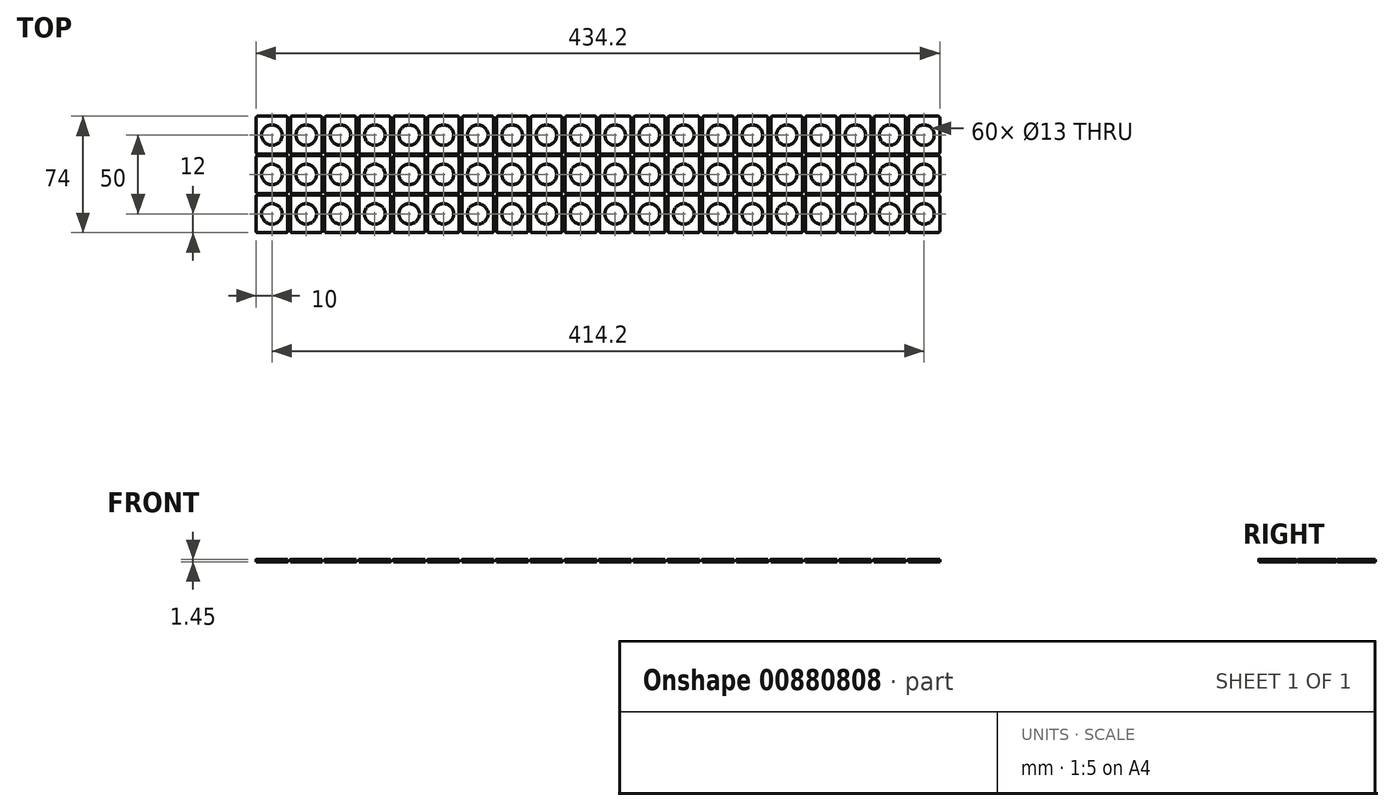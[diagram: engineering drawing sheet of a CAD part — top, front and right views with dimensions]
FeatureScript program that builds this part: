
annotation { "Feature Type Name" : "Feature", "Feature Type Description" : "" }
export const myFeature = defineFeature(function(context is Context, id is Id, definition is map)
    precondition{}
    {
        {
            var Q0;
            Q0=qCreatedBy(makeId("Top.planeOp"),FACE);
            var sketch = newSketch(context, id + "F0", { "sketchPlane" : qUnion([Q0])});
            skLineSegment(sketch, "E0.bottom", {"start": v(-234, 135) * mm, "end": v(-216, 135) * mm});
            skLineSegment(sketch, "E0.top", {"start": v(-234, 111) * mm, "end": v(-216, 111) * mm});
            skLineSegment(sketch, "E0.left", {"start": v(-235, 134) * mm, "end": v(-235, 112) * mm});
            skLineSegment(sketch, "E0.right", {"start": v(-215, 134) * mm, "end": v(-215, 112) * mm});
            skPoint(sketch, "E1.visualSharp", {"position": v(-215, 135) * mm});
            skArc(sketch, "E1.filletArc", {"start": v(-215, 134) * mm, "mid": v(-215.3, 134.7) * mm, "end": v(-216, 135) * mm});
            skPoint(sketch, "E2.visualSharp", {"position": v(-215, 111) * mm});
            skArc(sketch, "E2.filletArc", {"start": v(-216, 111) * mm, "mid": v(-215.3, 111.3) * mm, "end": v(-215, 112) * mm});
            skPoint(sketch, "E3.visualSharp", {"position": v(-235, 111) * mm});
            skArc(sketch, "E3.filletArc", {"start": v(-235, 112) * mm, "mid": v(-234.7, 111.3) * mm, "end": v(-234, 111) * mm});
            skPoint(sketch, "E4.visualSharp", {"position": v(-235, 135) * mm});
            skArc(sketch, "E4.filletArc", {"start": v(-234, 135) * mm, "mid": v(-234.7, 134.7) * mm, "end": v(-235, 134) * mm});
            skLineSegment(sketch, "E5", {"start": v(-215, 123) * mm, "end": v(-235, 123) * mm, "construction": true});
            skCircle(sketch, "E6", {"center": v(-225, 123) * mm, "radius": 6.5 * mm});
            skLineSegment(sketch, "E7.0.1.0", {"start": v(-215, 98) * mm, "end": v(-235, 98) * mm, "construction": true});
            skPoint(sketch, "E7.0.1.1", {"position": v(-235, 110) * mm});
            skLineSegment(sketch, "E7.0.1.2", {"start": v(-235, 109) * mm, "end": v(-235, 87) * mm});
            skPoint(sketch, "E7.0.1.3", {"position": v(-215, 110) * mm});
            skLineSegment(sketch, "E7.0.1.4", {"start": v(-234, 86) * mm, "end": v(-216, 86) * mm});
            skPoint(sketch, "E7.0.1.5", {"position": v(-235, 86) * mm});
            skPoint(sketch, "E7.0.1.6", {"position": v(-215, 86) * mm});
            skCircle(sketch, "E7.0.1.7", {"center": v(-225, 98) * mm, "radius": 6.5 * mm});
            skLineSegment(sketch, "E7.0.1.8", {"start": v(-234, 110) * mm, "end": v(-216, 110) * mm});
            skLineSegment(sketch, "E7.0.1.9", {"start": v(-215, 109) * mm, "end": v(-215, 87) * mm});
            skArc(sketch, "E7.0.1.10", {"start": v(-215, 109) * mm, "mid": v(-215.3, 109.7) * mm, "end": v(-216, 110) * mm});
            skArc(sketch, "E7.0.1.11", {"start": v(-216, 86) * mm, "mid": v(-215.3, 86.3) * mm, "end": v(-215, 87) * mm});
            skArc(sketch, "E7.0.1.12", {"start": v(-235, 87) * mm, "mid": v(-234.7, 86.3) * mm, "end": v(-234, 86) * mm});
            skArc(sketch, "E7.0.1.13", {"start": v(-234, 110) * mm, "mid": v(-234.7, 109.7) * mm, "end": v(-235, 109) * mm});
            skLineSegment(sketch, "E7.0.2.0", {"start": v(-215, 73) * mm, "end": v(-235, 73) * mm, "construction": true});
            skPoint(sketch, "E7.0.2.1", {"position": v(-235, 85) * mm});
            skLineSegment(sketch, "E7.0.2.2", {"start": v(-235, 84) * mm, "end": v(-235, 62) * mm});
            skPoint(sketch, "E7.0.2.3", {"position": v(-215, 85) * mm});
            skLineSegment(sketch, "E7.0.2.4", {"start": v(-234, 61) * mm, "end": v(-216, 61) * mm});
            skPoint(sketch, "E7.0.2.5", {"position": v(-235, 61) * mm});
            skPoint(sketch, "E7.0.2.6", {"position": v(-215, 61) * mm});
            skCircle(sketch, "E7.0.2.7", {"center": v(-225, 73) * mm, "radius": 6.5 * mm});
            skLineSegment(sketch, "E7.0.2.8", {"start": v(-234, 85) * mm, "end": v(-216, 85) * mm});
            skLineSegment(sketch, "E7.0.2.9", {"start": v(-215, 84) * mm, "end": v(-215, 62) * mm});
            skArc(sketch, "E7.0.2.10", {"start": v(-215, 84) * mm, "mid": v(-215.3, 84.7) * mm, "end": v(-216, 85) * mm});
            skArc(sketch, "E7.0.2.11", {"start": v(-216, 61) * mm, "mid": v(-215.3, 61.3) * mm, "end": v(-215, 62) * mm});
            skArc(sketch, "E7.0.2.12", {"start": v(-235, 62) * mm, "mid": v(-234.7, 61.3) * mm, "end": v(-234, 61) * mm});
            skArc(sketch, "E7.0.2.13", {"start": v(-234, 85) * mm, "mid": v(-234.7, 84.7) * mm, "end": v(-235, 84) * mm});
            skLineSegment(sketch, "E7.1.0.0", {"start": v(-193.2, 123) * mm, "end": v(-213.2, 123) * mm, "construction": true});
            skPoint(sketch, "E7.1.0.1", {"position": v(-213.2, 135) * mm});
            skLineSegment(sketch, "E7.1.0.2", {"start": v(-213.2, 134) * mm, "end": v(-213.2, 112) * mm});
            skPoint(sketch, "E7.1.0.3", {"position": v(-193.2, 135) * mm});
            skLineSegment(sketch, "E7.1.0.4", {"start": v(-212.2, 111) * mm, "end": v(-194.2, 111) * mm});
            skPoint(sketch, "E7.1.0.5", {"position": v(-213.2, 111) * mm});
            skPoint(sketch, "E7.1.0.6", {"position": v(-193.2, 111) * mm});
            skCircle(sketch, "E7.1.0.7", {"center": v(-203.2, 123) * mm, "radius": 6.5 * mm});
            skLineSegment(sketch, "E7.1.0.8", {"start": v(-212.2, 135) * mm, "end": v(-194.2, 135) * mm});
            skLineSegment(sketch, "E7.1.0.9", {"start": v(-193.2, 134) * mm, "end": v(-193.2, 112) * mm});
            skArc(sketch, "E7.1.0.10", {"start": v(-193.2, 134) * mm, "mid": v(-193.5, 134.7) * mm, "end": v(-194.2, 135) * mm});
            skArc(sketch, "E7.1.0.11", {"start": v(-194.2, 111) * mm, "mid": v(-193.5, 111.3) * mm, "end": v(-193.2, 112) * mm});
            skArc(sketch, "E7.1.0.12", {"start": v(-213.2, 112) * mm, "mid": v(-212.9, 111.3) * mm, "end": v(-212.2, 111) * mm});
            skArc(sketch, "E7.1.0.13", {"start": v(-212.2, 135) * mm, "mid": v(-212.9, 134.7) * mm, "end": v(-213.2, 134) * mm});
            skLineSegment(sketch, "E7.1.1.0", {"start": v(-193.2, 98) * mm, "end": v(-213.2, 98) * mm, "construction": true});
            skPoint(sketch, "E7.1.1.1", {"position": v(-213.2, 110) * mm});
            skLineSegment(sketch, "E7.1.1.2", {"start": v(-213.2, 109) * mm, "end": v(-213.2, 87) * mm});
            skPoint(sketch, "E7.1.1.3", {"position": v(-193.2, 110) * mm});
            skLineSegment(sketch, "E7.1.1.4", {"start": v(-212.2, 86) * mm, "end": v(-194.2, 86) * mm});
            skPoint(sketch, "E7.1.1.5", {"position": v(-213.2, 86) * mm});
            skPoint(sketch, "E7.1.1.6", {"position": v(-193.2, 86) * mm});
            skCircle(sketch, "E7.1.1.7", {"center": v(-203.2, 98) * mm, "radius": 6.5 * mm});
            skLineSegment(sketch, "E7.1.1.8", {"start": v(-212.2, 110) * mm, "end": v(-194.2, 110) * mm});
            skLineSegment(sketch, "E7.1.1.9", {"start": v(-193.2, 109) * mm, "end": v(-193.2, 87) * mm});
            skArc(sketch, "E7.1.1.10", {"start": v(-193.2, 109) * mm, "mid": v(-193.5, 109.7) * mm, "end": v(-194.2, 110) * mm});
            skArc(sketch, "E7.1.1.11", {"start": v(-194.2, 86) * mm, "mid": v(-193.5, 86.3) * mm, "end": v(-193.2, 87) * mm});
            skArc(sketch, "E7.1.1.12", {"start": v(-213.2, 87) * mm, "mid": v(-212.9, 86.3) * mm, "end": v(-212.2, 86) * mm});
            skArc(sketch, "E7.1.1.13", {"start": v(-212.2, 110) * mm, "mid": v(-212.9, 109.7) * mm, "end": v(-213.2, 109) * mm});
            skLineSegment(sketch, "E7.1.2.0", {"start": v(-193.2, 73) * mm, "end": v(-213.2, 73) * mm, "construction": true});
            skPoint(sketch, "E7.1.2.1", {"position": v(-213.2, 85) * mm});
            skLineSegment(sketch, "E7.1.2.2", {"start": v(-213.2, 84) * mm, "end": v(-213.2, 62) * mm});
            skPoint(sketch, "E7.1.2.3", {"position": v(-193.2, 85) * mm});
            skLineSegment(sketch, "E7.1.2.4", {"start": v(-212.2, 61) * mm, "end": v(-194.2, 61) * mm});
            skPoint(sketch, "E7.1.2.5", {"position": v(-213.2, 61) * mm});
            skPoint(sketch, "E7.1.2.6", {"position": v(-193.2, 61) * mm});
            skCircle(sketch, "E7.1.2.7", {"center": v(-203.2, 73) * mm, "radius": 6.5 * mm});
            skLineSegment(sketch, "E7.1.2.8", {"start": v(-212.2, 85) * mm, "end": v(-194.2, 85) * mm});
            skLineSegment(sketch, "E7.1.2.9", {"start": v(-193.2, 84) * mm, "end": v(-193.2, 62) * mm});
            skArc(sketch, "E7.1.2.10", {"start": v(-193.2, 84) * mm, "mid": v(-193.5, 84.7) * mm, "end": v(-194.2, 85) * mm});
            skArc(sketch, "E7.1.2.11", {"start": v(-194.2, 61) * mm, "mid": v(-193.5, 61.3) * mm, "end": v(-193.2, 62) * mm});
            skArc(sketch, "E7.1.2.12", {"start": v(-213.2, 62) * mm, "mid": v(-212.9, 61.3) * mm, "end": v(-212.2, 61) * mm});
            skArc(sketch, "E7.1.2.13", {"start": v(-212.2, 85) * mm, "mid": v(-212.9, 84.7) * mm, "end": v(-213.2, 84) * mm});
            skLineSegment(sketch, "E7.2.0.0", {"start": v(-171.4, 123) * mm, "end": v(-191.4, 123) * mm, "construction": true});
            skPoint(sketch, "E7.2.0.1", {"position": v(-191.4, 135) * mm});
            skLineSegment(sketch, "E7.2.0.2", {"start": v(-191.4, 134) * mm, "end": v(-191.4, 112) * mm});
            skPoint(sketch, "E7.2.0.3", {"position": v(-171.4, 135) * mm});
            skLineSegment(sketch, "E7.2.0.4", {"start": v(-190.4, 111) * mm, "end": v(-172.4, 111) * mm});
            skPoint(sketch, "E7.2.0.5", {"position": v(-191.4, 111) * mm});
            skPoint(sketch, "E7.2.0.6", {"position": v(-171.4, 111) * mm});
            skCircle(sketch, "E7.2.0.7", {"center": v(-181.4, 123) * mm, "radius": 6.5 * mm});
            skLineSegment(sketch, "E7.2.0.8", {"start": v(-190.4, 135) * mm, "end": v(-172.4, 135) * mm});
            skLineSegment(sketch, "E7.2.0.9", {"start": v(-171.4, 134) * mm, "end": v(-171.4, 112) * mm});
            skArc(sketch, "E7.2.0.10", {"start": v(-171.4, 134) * mm, "mid": v(-171.7, 134.7) * mm, "end": v(-172.4, 135) * mm});
            skArc(sketch, "E7.2.0.11", {"start": v(-172.4, 111) * mm, "mid": v(-171.7, 111.3) * mm, "end": v(-171.4, 112) * mm});
            skArc(sketch, "E7.2.0.12", {"start": v(-191.4, 112) * mm, "mid": v(-191.1, 111.3) * mm, "end": v(-190.4, 111) * mm});
            skArc(sketch, "E7.2.0.13", {"start": v(-190.4, 135) * mm, "mid": v(-191.1, 134.7) * mm, "end": v(-191.4, 134) * mm});
            skLineSegment(sketch, "E7.2.1.0", {"start": v(-171.4, 98) * mm, "end": v(-191.4, 98) * mm, "construction": true});
            skPoint(sketch, "E7.2.1.1", {"position": v(-191.4, 110) * mm});
            skLineSegment(sketch, "E7.2.1.2", {"start": v(-191.4, 109) * mm, "end": v(-191.4, 87) * mm});
            skPoint(sketch, "E7.2.1.3", {"position": v(-171.4, 110) * mm});
            skLineSegment(sketch, "E7.2.1.4", {"start": v(-190.4, 86) * mm, "end": v(-172.4, 86) * mm});
            skPoint(sketch, "E7.2.1.5", {"position": v(-191.4, 86) * mm});
            skPoint(sketch, "E7.2.1.6", {"position": v(-171.4, 86) * mm});
            skCircle(sketch, "E7.2.1.7", {"center": v(-181.4, 98) * mm, "radius": 6.5 * mm});
            skLineSegment(sketch, "E7.2.1.8", {"start": v(-190.4, 110) * mm, "end": v(-172.4, 110) * mm});
            skLineSegment(sketch, "E7.2.1.9", {"start": v(-171.4, 109) * mm, "end": v(-171.4, 87) * mm});
            skArc(sketch, "E7.2.1.10", {"start": v(-171.4, 109) * mm, "mid": v(-171.7, 109.7) * mm, "end": v(-172.4, 110) * mm});
            skArc(sketch, "E7.2.1.11", {"start": v(-172.4, 86) * mm, "mid": v(-171.7, 86.3) * mm, "end": v(-171.4, 87) * mm});
            skArc(sketch, "E7.2.1.12", {"start": v(-191.4, 87) * mm, "mid": v(-191.1, 86.3) * mm, "end": v(-190.4, 86) * mm});
            skArc(sketch, "E7.2.1.13", {"start": v(-190.4, 110) * mm, "mid": v(-191.1, 109.7) * mm, "end": v(-191.4, 109) * mm});
            skLineSegment(sketch, "E7.2.2.0", {"start": v(-171.4, 73) * mm, "end": v(-191.4, 73) * mm, "construction": true});
            skPoint(sketch, "E7.2.2.1", {"position": v(-191.4, 85) * mm});
            skLineSegment(sketch, "E7.2.2.2", {"start": v(-191.4, 84) * mm, "end": v(-191.4, 62) * mm});
            skPoint(sketch, "E7.2.2.3", {"position": v(-171.4, 85) * mm});
            skLineSegment(sketch, "E7.2.2.4", {"start": v(-190.4, 61) * mm, "end": v(-172.4, 61) * mm});
            skPoint(sketch, "E7.2.2.5", {"position": v(-191.4, 61) * mm});
            skPoint(sketch, "E7.2.2.6", {"position": v(-171.4, 61) * mm});
            skCircle(sketch, "E7.2.2.7", {"center": v(-181.4, 73) * mm, "radius": 6.5 * mm});
            skLineSegment(sketch, "E7.2.2.8", {"start": v(-190.4, 85) * mm, "end": v(-172.4, 85) * mm});
            skLineSegment(sketch, "E7.2.2.9", {"start": v(-171.4, 84) * mm, "end": v(-171.4, 62) * mm});
            skArc(sketch, "E7.2.2.10", {"start": v(-171.4, 84) * mm, "mid": v(-171.7, 84.7) * mm, "end": v(-172.4, 85) * mm});
            skArc(sketch, "E7.2.2.11", {"start": v(-172.4, 61) * mm, "mid": v(-171.7, 61.3) * mm, "end": v(-171.4, 62) * mm});
            skArc(sketch, "E7.2.2.12", {"start": v(-191.4, 62) * mm, "mid": v(-191.1, 61.3) * mm, "end": v(-190.4, 61) * mm});
            skArc(sketch, "E7.2.2.13", {"start": v(-190.4, 85) * mm, "mid": v(-191.1, 84.7) * mm, "end": v(-191.4, 84) * mm});
            skLineSegment(sketch, "E7.3.0.0", {"start": v(-149.6, 123) * mm, "end": v(-169.6, 123) * mm, "construction": true});
            skPoint(sketch, "E7.3.0.1", {"position": v(-169.6, 135) * mm});
            skLineSegment(sketch, "E7.3.0.2", {"start": v(-169.6, 134) * mm, "end": v(-169.6, 112) * mm});
            skPoint(sketch, "E7.3.0.3", {"position": v(-149.6, 135) * mm});
            skLineSegment(sketch, "E7.3.0.4", {"start": v(-168.6, 111) * mm, "end": v(-150.6, 111) * mm});
            skPoint(sketch, "E7.3.0.5", {"position": v(-169.6, 111) * mm});
            skPoint(sketch, "E7.3.0.6", {"position": v(-149.6, 111) * mm});
            skCircle(sketch, "E7.3.0.7", {"center": v(-159.6, 123) * mm, "radius": 6.5 * mm});
            skLineSegment(sketch, "E7.3.0.8", {"start": v(-168.6, 135) * mm, "end": v(-150.6, 135) * mm});
            skLineSegment(sketch, "E7.3.0.9", {"start": v(-149.6, 134) * mm, "end": v(-149.6, 112) * mm});
            skArc(sketch, "E7.3.0.10", {"start": v(-149.6, 134) * mm, "mid": v(-149.9, 134.7) * mm, "end": v(-150.6, 135) * mm});
            skArc(sketch, "E7.3.0.11", {"start": v(-150.6, 111) * mm, "mid": v(-149.9, 111.3) * mm, "end": v(-149.6, 112) * mm});
            skArc(sketch, "E7.3.0.12", {"start": v(-169.6, 112) * mm, "mid": v(-169.3, 111.3) * mm, "end": v(-168.6, 111) * mm});
            skArc(sketch, "E7.3.0.13", {"start": v(-168.6, 135) * mm, "mid": v(-169.3, 134.7) * mm, "end": v(-169.6, 134) * mm});
            skLineSegment(sketch, "E7.3.1.0", {"start": v(-149.6, 98) * mm, "end": v(-169.6, 98) * mm, "construction": true});
            skPoint(sketch, "E7.3.1.1", {"position": v(-169.6, 110) * mm});
            skLineSegment(sketch, "E7.3.1.2", {"start": v(-169.6, 109) * mm, "end": v(-169.6, 87) * mm});
            skPoint(sketch, "E7.3.1.3", {"position": v(-149.6, 110) * mm});
            skLineSegment(sketch, "E7.3.1.4", {"start": v(-168.6, 86) * mm, "end": v(-150.6, 86) * mm});
            skPoint(sketch, "E7.3.1.5", {"position": v(-169.6, 86) * mm});
            skPoint(sketch, "E7.3.1.6", {"position": v(-149.6, 86) * mm});
            skCircle(sketch, "E7.3.1.7", {"center": v(-159.6, 98) * mm, "radius": 6.5 * mm});
            skLineSegment(sketch, "E7.3.1.8", {"start": v(-168.6, 110) * mm, "end": v(-150.6, 110) * mm});
            skLineSegment(sketch, "E7.3.1.9", {"start": v(-149.6, 109) * mm, "end": v(-149.6, 87) * mm});
            skArc(sketch, "E7.3.1.10", {"start": v(-149.6, 109) * mm, "mid": v(-149.9, 109.7) * mm, "end": v(-150.6, 110) * mm});
            skArc(sketch, "E7.3.1.11", {"start": v(-150.6, 86) * mm, "mid": v(-149.9, 86.3) * mm, "end": v(-149.6, 87) * mm});
            skArc(sketch, "E7.3.1.12", {"start": v(-169.6, 87) * mm, "mid": v(-169.3, 86.3) * mm, "end": v(-168.6, 86) * mm});
            skArc(sketch, "E7.3.1.13", {"start": v(-168.6, 110) * mm, "mid": v(-169.3, 109.7) * mm, "end": v(-169.6, 109) * mm});
            skLineSegment(sketch, "E7.3.2.0", {"start": v(-149.6, 73) * mm, "end": v(-169.6, 73) * mm, "construction": true});
            skPoint(sketch, "E7.3.2.1", {"position": v(-169.6, 85) * mm});
            skLineSegment(sketch, "E7.3.2.2", {"start": v(-169.6, 84) * mm, "end": v(-169.6, 62) * mm});
            skPoint(sketch, "E7.3.2.3", {"position": v(-149.6, 85) * mm});
            skLineSegment(sketch, "E7.3.2.4", {"start": v(-168.6, 61) * mm, "end": v(-150.6, 61) * mm});
            skPoint(sketch, "E7.3.2.5", {"position": v(-169.6, 61) * mm});
            skPoint(sketch, "E7.3.2.6", {"position": v(-149.6, 61) * mm});
            skCircle(sketch, "E7.3.2.7", {"center": v(-159.6, 73) * mm, "radius": 6.5 * mm});
            skLineSegment(sketch, "E7.3.2.8", {"start": v(-168.6, 85) * mm, "end": v(-150.6, 85) * mm});
            skLineSegment(sketch, "E7.3.2.9", {"start": v(-149.6, 84) * mm, "end": v(-149.6, 62) * mm});
            skArc(sketch, "E7.3.2.10", {"start": v(-149.6, 84) * mm, "mid": v(-149.9, 84.7) * mm, "end": v(-150.6, 85) * mm});
            skArc(sketch, "E7.3.2.11", {"start": v(-150.6, 61) * mm, "mid": v(-149.9, 61.3) * mm, "end": v(-149.6, 62) * mm});
            skArc(sketch, "E7.3.2.12", {"start": v(-169.6, 62) * mm, "mid": v(-169.3, 61.3) * mm, "end": v(-168.6, 61) * mm});
            skArc(sketch, "E7.3.2.13", {"start": v(-168.6, 85) * mm, "mid": v(-169.3, 84.7) * mm, "end": v(-169.6, 84) * mm});
            skLineSegment(sketch, "E7.4.0.0", {"start": v(-127.8, 123) * mm, "end": v(-147.8, 123) * mm, "construction": true});
            skPoint(sketch, "E7.4.0.1", {"position": v(-147.8, 135) * mm});
            skLineSegment(sketch, "E7.4.0.2", {"start": v(-147.8, 134) * mm, "end": v(-147.8, 112) * mm});
            skPoint(sketch, "E7.4.0.3", {"position": v(-127.8, 135) * mm});
            skLineSegment(sketch, "E7.4.0.4", {"start": v(-146.8, 111) * mm, "end": v(-128.8, 111) * mm});
            skPoint(sketch, "E7.4.0.5", {"position": v(-147.8, 111) * mm});
            skPoint(sketch, "E7.4.0.6", {"position": v(-127.8, 111) * mm});
            skCircle(sketch, "E7.4.0.7", {"center": v(-137.8, 123) * mm, "radius": 6.5 * mm});
            skLineSegment(sketch, "E7.4.0.8", {"start": v(-146.8, 135) * mm, "end": v(-128.8, 135) * mm});
            skLineSegment(sketch, "E7.4.0.9", {"start": v(-127.8, 134) * mm, "end": v(-127.8, 112) * mm});
            skArc(sketch, "E7.4.0.10", {"start": v(-127.8, 134) * mm, "mid": v(-128.1, 134.7) * mm, "end": v(-128.8, 135) * mm});
            skArc(sketch, "E7.4.0.11", {"start": v(-128.8, 111) * mm, "mid": v(-128.1, 111.3) * mm, "end": v(-127.8, 112) * mm});
            skArc(sketch, "E7.4.0.12", {"start": v(-147.8, 112) * mm, "mid": v(-147.5, 111.3) * mm, "end": v(-146.8, 111) * mm});
            skArc(sketch, "E7.4.0.13", {"start": v(-146.8, 135) * mm, "mid": v(-147.5, 134.7) * mm, "end": v(-147.8, 134) * mm});
            skLineSegment(sketch, "E7.4.1.0", {"start": v(-127.8, 98) * mm, "end": v(-147.8, 98) * mm, "construction": true});
            skPoint(sketch, "E7.4.1.1", {"position": v(-147.8, 110) * mm});
            skLineSegment(sketch, "E7.4.1.2", {"start": v(-147.8, 109) * mm, "end": v(-147.8, 87) * mm});
            skPoint(sketch, "E7.4.1.3", {"position": v(-127.8, 110) * mm});
            skLineSegment(sketch, "E7.4.1.4", {"start": v(-146.8, 86) * mm, "end": v(-128.8, 86) * mm});
            skPoint(sketch, "E7.4.1.5", {"position": v(-147.8, 86) * mm});
            skPoint(sketch, "E7.4.1.6", {"position": v(-127.8, 86) * mm});
            skCircle(sketch, "E7.4.1.7", {"center": v(-137.8, 98) * mm, "radius": 6.5 * mm});
            skLineSegment(sketch, "E7.4.1.8", {"start": v(-146.8, 110) * mm, "end": v(-128.8, 110) * mm});
            skLineSegment(sketch, "E7.4.1.9", {"start": v(-127.8, 109) * mm, "end": v(-127.8, 87) * mm});
            skArc(sketch, "E7.4.1.10", {"start": v(-127.8, 109) * mm, "mid": v(-128.1, 109.7) * mm, "end": v(-128.8, 110) * mm});
            skArc(sketch, "E7.4.1.11", {"start": v(-128.8, 86) * mm, "mid": v(-128.1, 86.3) * mm, "end": v(-127.8, 87) * mm});
            skArc(sketch, "E7.4.1.12", {"start": v(-147.8, 87) * mm, "mid": v(-147.5, 86.3) * mm, "end": v(-146.8, 86) * mm});
            skArc(sketch, "E7.4.1.13", {"start": v(-146.8, 110) * mm, "mid": v(-147.5, 109.7) * mm, "end": v(-147.8, 109) * mm});
            skLineSegment(sketch, "E7.4.2.0", {"start": v(-127.8, 73) * mm, "end": v(-147.8, 73) * mm, "construction": true});
            skPoint(sketch, "E7.4.2.1", {"position": v(-147.8, 85) * mm});
            skLineSegment(sketch, "E7.4.2.2", {"start": v(-147.8, 84) * mm, "end": v(-147.8, 62) * mm});
            skPoint(sketch, "E7.4.2.3", {"position": v(-127.8, 85) * mm});
            skLineSegment(sketch, "E7.4.2.4", {"start": v(-146.8, 61) * mm, "end": v(-128.8, 61) * mm});
            skPoint(sketch, "E7.4.2.5", {"position": v(-147.8, 61) * mm});
            skPoint(sketch, "E7.4.2.6", {"position": v(-127.8, 61) * mm});
            skCircle(sketch, "E7.4.2.7", {"center": v(-137.8, 73) * mm, "radius": 6.5 * mm});
            skLineSegment(sketch, "E7.4.2.8", {"start": v(-146.8, 85) * mm, "end": v(-128.8, 85) * mm});
            skLineSegment(sketch, "E7.4.2.9", {"start": v(-127.8, 84) * mm, "end": v(-127.8, 62) * mm});
            skArc(sketch, "E7.4.2.10", {"start": v(-127.8, 84) * mm, "mid": v(-128.1, 84.7) * mm, "end": v(-128.8, 85) * mm});
            skArc(sketch, "E7.4.2.11", {"start": v(-128.8, 61) * mm, "mid": v(-128.1, 61.3) * mm, "end": v(-127.8, 62) * mm});
            skArc(sketch, "E7.4.2.12", {"start": v(-147.8, 62) * mm, "mid": v(-147.5, 61.3) * mm, "end": v(-146.8, 61) * mm});
            skArc(sketch, "E7.4.2.13", {"start": v(-146.8, 85) * mm, "mid": v(-147.5, 84.7) * mm, "end": v(-147.8, 84) * mm});
            skLineSegment(sketch, "E7.5.0.0", {"start": v(-106, 123) * mm, "end": v(-126, 123) * mm, "construction": true});
            skPoint(sketch, "E7.5.0.1", {"position": v(-126, 135) * mm});
            skLineSegment(sketch, "E7.5.0.2", {"start": v(-126, 134) * mm, "end": v(-126, 112) * mm});
            skPoint(sketch, "E7.5.0.3", {"position": v(-106, 135) * mm});
            skLineSegment(sketch, "E7.5.0.4", {"start": v(-125, 111) * mm, "end": v(-107, 111) * mm});
            skPoint(sketch, "E7.5.0.5", {"position": v(-126, 111) * mm});
            skPoint(sketch, "E7.5.0.6", {"position": v(-106, 111) * mm});
            skCircle(sketch, "E7.5.0.7", {"center": v(-116, 123) * mm, "radius": 6.5 * mm});
            skLineSegment(sketch, "E7.5.0.8", {"start": v(-125, 135) * mm, "end": v(-107, 135) * mm});
            skLineSegment(sketch, "E7.5.0.9", {"start": v(-106, 134) * mm, "end": v(-106, 112) * mm});
            skArc(sketch, "E7.5.0.10", {"start": v(-106, 134) * mm, "mid": v(-106.3, 134.7) * mm, "end": v(-107, 135) * mm});
            skArc(sketch, "E7.5.0.11", {"start": v(-107, 111) * mm, "mid": v(-106.3, 111.3) * mm, "end": v(-106, 112) * mm});
            skArc(sketch, "E7.5.0.12", {"start": v(-126, 112) * mm, "mid": v(-125.7, 111.3) * mm, "end": v(-125, 111) * mm});
            skArc(sketch, "E7.5.0.13", {"start": v(-125, 135) * mm, "mid": v(-125.7, 134.7) * mm, "end": v(-126, 134) * mm});
            skLineSegment(sketch, "E7.5.1.0", {"start": v(-106, 98) * mm, "end": v(-126, 98) * mm, "construction": true});
            skPoint(sketch, "E7.5.1.1", {"position": v(-126, 110) * mm});
            skLineSegment(sketch, "E7.5.1.2", {"start": v(-126, 109) * mm, "end": v(-126, 87) * mm});
            skPoint(sketch, "E7.5.1.3", {"position": v(-106, 110) * mm});
            skLineSegment(sketch, "E7.5.1.4", {"start": v(-125, 86) * mm, "end": v(-107, 86) * mm});
            skPoint(sketch, "E7.5.1.5", {"position": v(-126, 86) * mm});
            skPoint(sketch, "E7.5.1.6", {"position": v(-106, 86) * mm});
            skCircle(sketch, "E7.5.1.7", {"center": v(-116, 98) * mm, "radius": 6.5 * mm});
            skLineSegment(sketch, "E7.5.1.8", {"start": v(-125, 110) * mm, "end": v(-107, 110) * mm});
            skLineSegment(sketch, "E7.5.1.9", {"start": v(-106, 109) * mm, "end": v(-106, 87) * mm});
            skArc(sketch, "E7.5.1.10", {"start": v(-106, 109) * mm, "mid": v(-106.3, 109.7) * mm, "end": v(-107, 110) * mm});
            skArc(sketch, "E7.5.1.11", {"start": v(-107, 86) * mm, "mid": v(-106.3, 86.3) * mm, "end": v(-106, 87) * mm});
            skArc(sketch, "E7.5.1.12", {"start": v(-126, 87) * mm, "mid": v(-125.7, 86.3) * mm, "end": v(-125, 86) * mm});
            skArc(sketch, "E7.5.1.13", {"start": v(-125, 110) * mm, "mid": v(-125.7, 109.7) * mm, "end": v(-126, 109) * mm});
            skLineSegment(sketch, "E7.5.2.0", {"start": v(-106, 73) * mm, "end": v(-126, 73) * mm, "construction": true});
            skPoint(sketch, "E7.5.2.1", {"position": v(-126, 85) * mm});
            skLineSegment(sketch, "E7.5.2.2", {"start": v(-126, 84) * mm, "end": v(-126, 62) * mm});
            skPoint(sketch, "E7.5.2.3", {"position": v(-106, 85) * mm});
            skLineSegment(sketch, "E7.5.2.4", {"start": v(-125, 61) * mm, "end": v(-107, 61) * mm});
            skPoint(sketch, "E7.5.2.5", {"position": v(-126, 61) * mm});
            skPoint(sketch, "E7.5.2.6", {"position": v(-106, 61) * mm});
            skCircle(sketch, "E7.5.2.7", {"center": v(-116, 73) * mm, "radius": 6.5 * mm});
            skLineSegment(sketch, "E7.5.2.8", {"start": v(-125, 85) * mm, "end": v(-107, 85) * mm});
            skLineSegment(sketch, "E7.5.2.9", {"start": v(-106, 84) * mm, "end": v(-106, 62) * mm});
            skArc(sketch, "E7.5.2.10", {"start": v(-106, 84) * mm, "mid": v(-106.3, 84.7) * mm, "end": v(-107, 85) * mm});
            skArc(sketch, "E7.5.2.11", {"start": v(-107, 61) * mm, "mid": v(-106.3, 61.3) * mm, "end": v(-106, 62) * mm});
            skArc(sketch, "E7.5.2.12", {"start": v(-126, 62) * mm, "mid": v(-125.7, 61.3) * mm, "end": v(-125, 61) * mm});
            skArc(sketch, "E7.5.2.13", {"start": v(-125, 85) * mm, "mid": v(-125.7, 84.7) * mm, "end": v(-126, 84) * mm});
            skLineSegment(sketch, "E7.6.0.0", {"start": v(-84.2, 123) * mm, "end": v(-104.2, 123) * mm, "construction": true});
            skPoint(sketch, "E7.6.0.1", {"position": v(-104.2, 135) * mm});
            skLineSegment(sketch, "E7.6.0.2", {"start": v(-104.2, 134) * mm, "end": v(-104.2, 112) * mm});
            skPoint(sketch, "E7.6.0.3", {"position": v(-84.2, 135) * mm});
            skLineSegment(sketch, "E7.6.0.4", {"start": v(-103.2, 111) * mm, "end": v(-85.2, 111) * mm});
            skPoint(sketch, "E7.6.0.5", {"position": v(-104.2, 111) * mm});
            skPoint(sketch, "E7.6.0.6", {"position": v(-84.2, 111) * mm});
            skCircle(sketch, "E7.6.0.7", {"center": v(-94.2, 123) * mm, "radius": 6.5 * mm});
            skLineSegment(sketch, "E7.6.0.8", {"start": v(-103.2, 135) * mm, "end": v(-85.2, 135) * mm});
            skLineSegment(sketch, "E7.6.0.9", {"start": v(-84.2, 134) * mm, "end": v(-84.2, 112) * mm});
            skArc(sketch, "E7.6.0.10", {"start": v(-84.2, 134) * mm, "mid": v(-84.5, 134.7) * mm, "end": v(-85.2, 135) * mm});
            skArc(sketch, "E7.6.0.11", {"start": v(-85.2, 111) * mm, "mid": v(-84.5, 111.3) * mm, "end": v(-84.2, 112) * mm});
            skArc(sketch, "E7.6.0.12", {"start": v(-104.2, 112) * mm, "mid": v(-103.9, 111.3) * mm, "end": v(-103.2, 111) * mm});
            skArc(sketch, "E7.6.0.13", {"start": v(-103.2, 135) * mm, "mid": v(-103.9, 134.7) * mm, "end": v(-104.2, 134) * mm});
            skLineSegment(sketch, "E7.6.1.0", {"start": v(-84.2, 98) * mm, "end": v(-104.2, 98) * mm, "construction": true});
            skPoint(sketch, "E7.6.1.1", {"position": v(-104.2, 110) * mm});
            skLineSegment(sketch, "E7.6.1.2", {"start": v(-104.2, 109) * mm, "end": v(-104.2, 87) * mm});
            skPoint(sketch, "E7.6.1.3", {"position": v(-84.2, 110) * mm});
            skLineSegment(sketch, "E7.6.1.4", {"start": v(-103.2, 86) * mm, "end": v(-85.2, 86) * mm});
            skPoint(sketch, "E7.6.1.5", {"position": v(-104.2, 86) * mm});
            skPoint(sketch, "E7.6.1.6", {"position": v(-84.2, 86) * mm});
            skCircle(sketch, "E7.6.1.7", {"center": v(-94.2, 98) * mm, "radius": 6.5 * mm});
            skLineSegment(sketch, "E7.6.1.8", {"start": v(-103.2, 110) * mm, "end": v(-85.2, 110) * mm});
            skLineSegment(sketch, "E7.6.1.9", {"start": v(-84.2, 109) * mm, "end": v(-84.2, 87) * mm});
            skArc(sketch, "E7.6.1.10", {"start": v(-84.2, 109) * mm, "mid": v(-84.5, 109.7) * mm, "end": v(-85.2, 110) * mm});
            skArc(sketch, "E7.6.1.11", {"start": v(-85.2, 86) * mm, "mid": v(-84.5, 86.3) * mm, "end": v(-84.2, 87) * mm});
            skArc(sketch, "E7.6.1.12", {"start": v(-104.2, 87) * mm, "mid": v(-103.9, 86.3) * mm, "end": v(-103.2, 86) * mm});
            skArc(sketch, "E7.6.1.13", {"start": v(-103.2, 110) * mm, "mid": v(-103.9, 109.7) * mm, "end": v(-104.2, 109) * mm});
            skLineSegment(sketch, "E7.6.2.0", {"start": v(-84.2, 73) * mm, "end": v(-104.2, 73) * mm, "construction": true});
            skPoint(sketch, "E7.6.2.1", {"position": v(-104.2, 85) * mm});
            skLineSegment(sketch, "E7.6.2.2", {"start": v(-104.2, 84) * mm, "end": v(-104.2, 62) * mm});
            skPoint(sketch, "E7.6.2.3", {"position": v(-84.2, 85) * mm});
            skLineSegment(sketch, "E7.6.2.4", {"start": v(-103.2, 61) * mm, "end": v(-85.2, 61) * mm});
            skPoint(sketch, "E7.6.2.5", {"position": v(-104.2, 61) * mm});
            skPoint(sketch, "E7.6.2.6", {"position": v(-84.2, 61) * mm});
            skCircle(sketch, "E7.6.2.7", {"center": v(-94.2, 73) * mm, "radius": 6.5 * mm});
            skLineSegment(sketch, "E7.6.2.8", {"start": v(-103.2, 85) * mm, "end": v(-85.2, 85) * mm});
            skLineSegment(sketch, "E7.6.2.9", {"start": v(-84.2, 84) * mm, "end": v(-84.2, 62) * mm});
            skArc(sketch, "E7.6.2.10", {"start": v(-84.2, 84) * mm, "mid": v(-84.5, 84.7) * mm, "end": v(-85.2, 85) * mm});
            skArc(sketch, "E7.6.2.11", {"start": v(-85.2, 61) * mm, "mid": v(-84.5, 61.3) * mm, "end": v(-84.2, 62) * mm});
            skArc(sketch, "E7.6.2.12", {"start": v(-104.2, 62) * mm, "mid": v(-103.9, 61.3) * mm, "end": v(-103.2, 61) * mm});
            skArc(sketch, "E7.6.2.13", {"start": v(-103.2, 85) * mm, "mid": v(-103.9, 84.7) * mm, "end": v(-104.2, 84) * mm});
            skLineSegment(sketch, "E7.7.0.0", {"start": v(-62.4, 123) * mm, "end": v(-82.4, 123) * mm, "construction": true});
            skPoint(sketch, "E7.7.0.1", {"position": v(-82.4, 135) * mm});
            skLineSegment(sketch, "E7.7.0.2", {"start": v(-82.4, 134) * mm, "end": v(-82.4, 112) * mm});
            skPoint(sketch, "E7.7.0.3", {"position": v(-62.4, 135) * mm});
            skLineSegment(sketch, "E7.7.0.4", {"start": v(-81.4, 111) * mm, "end": v(-63.4, 111) * mm});
            skPoint(sketch, "E7.7.0.5", {"position": v(-82.4, 111) * mm});
            skPoint(sketch, "E7.7.0.6", {"position": v(-62.4, 111) * mm});
            skCircle(sketch, "E7.7.0.7", {"center": v(-72.4, 123) * mm, "radius": 6.5 * mm});
            skLineSegment(sketch, "E7.7.0.8", {"start": v(-81.4, 135) * mm, "end": v(-63.4, 135) * mm});
            skLineSegment(sketch, "E7.7.0.9", {"start": v(-62.4, 134) * mm, "end": v(-62.4, 112) * mm});
            skArc(sketch, "E7.7.0.10", {"start": v(-62.4, 134) * mm, "mid": v(-62.7, 134.7) * mm, "end": v(-63.4, 135) * mm});
            skArc(sketch, "E7.7.0.11", {"start": v(-63.4, 111) * mm, "mid": v(-62.7, 111.3) * mm, "end": v(-62.4, 112) * mm});
            skArc(sketch, "E7.7.0.12", {"start": v(-82.4, 112) * mm, "mid": v(-82.1, 111.3) * mm, "end": v(-81.4, 111) * mm});
            skArc(sketch, "E7.7.0.13", {"start": v(-81.4, 135) * mm, "mid": v(-82.1, 134.7) * mm, "end": v(-82.4, 134) * mm});
            skLineSegment(sketch, "E7.7.1.0", {"start": v(-62.4, 98) * mm, "end": v(-82.4, 98) * mm, "construction": true});
            skPoint(sketch, "E7.7.1.1", {"position": v(-82.4, 110) * mm});
            skLineSegment(sketch, "E7.7.1.2", {"start": v(-82.4, 109) * mm, "end": v(-82.4, 87) * mm});
            skPoint(sketch, "E7.7.1.3", {"position": v(-62.4, 110) * mm});
            skLineSegment(sketch, "E7.7.1.4", {"start": v(-81.4, 86) * mm, "end": v(-63.4, 86) * mm});
            skPoint(sketch, "E7.7.1.5", {"position": v(-82.4, 86) * mm});
            skPoint(sketch, "E7.7.1.6", {"position": v(-62.4, 86) * mm});
            skCircle(sketch, "E7.7.1.7", {"center": v(-72.4, 98) * mm, "radius": 6.5 * mm});
            skLineSegment(sketch, "E7.7.1.8", {"start": v(-81.4, 110) * mm, "end": v(-63.4, 110) * mm});
            skLineSegment(sketch, "E7.7.1.9", {"start": v(-62.4, 109) * mm, "end": v(-62.4, 87) * mm});
            skArc(sketch, "E7.7.1.10", {"start": v(-62.4, 109) * mm, "mid": v(-62.7, 109.7) * mm, "end": v(-63.4, 110) * mm});
            skArc(sketch, "E7.7.1.11", {"start": v(-63.4, 86) * mm, "mid": v(-62.7, 86.3) * mm, "end": v(-62.4, 87) * mm});
            skArc(sketch, "E7.7.1.12", {"start": v(-82.4, 87) * mm, "mid": v(-82.1, 86.3) * mm, "end": v(-81.4, 86) * mm});
            skArc(sketch, "E7.7.1.13", {"start": v(-81.4, 110) * mm, "mid": v(-82.1, 109.7) * mm, "end": v(-82.4, 109) * mm});
            skLineSegment(sketch, "E7.7.2.0", {"start": v(-62.4, 73) * mm, "end": v(-82.4, 73) * mm, "construction": true});
            skPoint(sketch, "E7.7.2.1", {"position": v(-82.4, 85) * mm});
            skLineSegment(sketch, "E7.7.2.2", {"start": v(-82.4, 84) * mm, "end": v(-82.4, 62) * mm});
            skPoint(sketch, "E7.7.2.3", {"position": v(-62.4, 85) * mm});
            skLineSegment(sketch, "E7.7.2.4", {"start": v(-81.4, 61) * mm, "end": v(-63.4, 61) * mm});
            skPoint(sketch, "E7.7.2.5", {"position": v(-82.4, 61) * mm});
            skPoint(sketch, "E7.7.2.6", {"position": v(-62.4, 61) * mm});
            skCircle(sketch, "E7.7.2.7", {"center": v(-72.4, 73) * mm, "radius": 6.5 * mm});
            skLineSegment(sketch, "E7.7.2.8", {"start": v(-81.4, 85) * mm, "end": v(-63.4, 85) * mm});
            skLineSegment(sketch, "E7.7.2.9", {"start": v(-62.4, 84) * mm, "end": v(-62.4, 62) * mm});
            skArc(sketch, "E7.7.2.10", {"start": v(-62.4, 84) * mm, "mid": v(-62.7, 84.7) * mm, "end": v(-63.4, 85) * mm});
            skArc(sketch, "E7.7.2.11", {"start": v(-63.4, 61) * mm, "mid": v(-62.7, 61.3) * mm, "end": v(-62.4, 62) * mm});
            skArc(sketch, "E7.7.2.12", {"start": v(-82.4, 62) * mm, "mid": v(-82.1, 61.3) * mm, "end": v(-81.4, 61) * mm});
            skArc(sketch, "E7.7.2.13", {"start": v(-81.4, 85) * mm, "mid": v(-82.1, 84.7) * mm, "end": v(-82.4, 84) * mm});
            skLineSegment(sketch, "E7.8.0.0", {"start": v(-40.6, 123) * mm, "end": v(-60.6, 123) * mm, "construction": true});
            skPoint(sketch, "E7.8.0.1", {"position": v(-60.6, 135) * mm});
            skLineSegment(sketch, "E7.8.0.2", {"start": v(-60.6, 134) * mm, "end": v(-60.6, 112) * mm});
            skPoint(sketch, "E7.8.0.3", {"position": v(-40.6, 135) * mm});
            skLineSegment(sketch, "E7.8.0.4", {"start": v(-59.6, 111) * mm, "end": v(-41.6, 111) * mm});
            skPoint(sketch, "E7.8.0.5", {"position": v(-60.6, 111) * mm});
            skPoint(sketch, "E7.8.0.6", {"position": v(-40.6, 111) * mm});
            skCircle(sketch, "E7.8.0.7", {"center": v(-50.6, 123) * mm, "radius": 6.5 * mm});
            skLineSegment(sketch, "E7.8.0.8", {"start": v(-59.6, 135) * mm, "end": v(-41.6, 135) * mm});
            skLineSegment(sketch, "E7.8.0.9", {"start": v(-40.6, 134) * mm, "end": v(-40.6, 112) * mm});
            skArc(sketch, "E7.8.0.10", {"start": v(-40.6, 134) * mm, "mid": v(-40.9, 134.7) * mm, "end": v(-41.6, 135) * mm});
            skArc(sketch, "E7.8.0.11", {"start": v(-41.6, 111) * mm, "mid": v(-40.9, 111.3) * mm, "end": v(-40.6, 112) * mm});
            skArc(sketch, "E7.8.0.12", {"start": v(-60.6, 112) * mm, "mid": v(-60.3, 111.3) * mm, "end": v(-59.6, 111) * mm});
            skArc(sketch, "E7.8.0.13", {"start": v(-59.6, 135) * mm, "mid": v(-60.3, 134.7) * mm, "end": v(-60.6, 134) * mm});
            skLineSegment(sketch, "E7.8.1.0", {"start": v(-40.6, 98) * mm, "end": v(-60.6, 98) * mm, "construction": true});
            skPoint(sketch, "E7.8.1.1", {"position": v(-60.6, 110) * mm});
            skLineSegment(sketch, "E7.8.1.2", {"start": v(-60.6, 109) * mm, "end": v(-60.6, 87) * mm});
            skPoint(sketch, "E7.8.1.3", {"position": v(-40.6, 110) * mm});
            skLineSegment(sketch, "E7.8.1.4", {"start": v(-59.6, 86) * mm, "end": v(-41.6, 86) * mm});
            skPoint(sketch, "E7.8.1.5", {"position": v(-60.6, 86) * mm});
            skPoint(sketch, "E7.8.1.6", {"position": v(-40.6, 86) * mm});
            skCircle(sketch, "E7.8.1.7", {"center": v(-50.6, 98) * mm, "radius": 6.5 * mm});
            skLineSegment(sketch, "E7.8.1.8", {"start": v(-59.6, 110) * mm, "end": v(-41.6, 110) * mm});
            skLineSegment(sketch, "E7.8.1.9", {"start": v(-40.6, 109) * mm, "end": v(-40.6, 87) * mm});
            skArc(sketch, "E7.8.1.10", {"start": v(-40.6, 109) * mm, "mid": v(-40.9, 109.7) * mm, "end": v(-41.6, 110) * mm});
            skArc(sketch, "E7.8.1.11", {"start": v(-41.6, 86) * mm, "mid": v(-40.9, 86.3) * mm, "end": v(-40.6, 87) * mm});
            skArc(sketch, "E7.8.1.12", {"start": v(-60.6, 87) * mm, "mid": v(-60.3, 86.3) * mm, "end": v(-59.6, 86) * mm});
            skArc(sketch, "E7.8.1.13", {"start": v(-59.6, 110) * mm, "mid": v(-60.3, 109.7) * mm, "end": v(-60.6, 109) * mm});
            skLineSegment(sketch, "E7.8.2.0", {"start": v(-40.6, 73) * mm, "end": v(-60.6, 73) * mm, "construction": true});
            skPoint(sketch, "E7.8.2.1", {"position": v(-60.6, 85) * mm});
            skLineSegment(sketch, "E7.8.2.2", {"start": v(-60.6, 84) * mm, "end": v(-60.6, 62) * mm});
            skPoint(sketch, "E7.8.2.3", {"position": v(-40.6, 85) * mm});
            skLineSegment(sketch, "E7.8.2.4", {"start": v(-59.6, 61) * mm, "end": v(-41.6, 61) * mm});
            skPoint(sketch, "E7.8.2.5", {"position": v(-60.6, 61) * mm});
            skPoint(sketch, "E7.8.2.6", {"position": v(-40.6, 61) * mm});
            skCircle(sketch, "E7.8.2.7", {"center": v(-50.6, 73) * mm, "radius": 6.5 * mm});
            skLineSegment(sketch, "E7.8.2.8", {"start": v(-59.6, 85) * mm, "end": v(-41.6, 85) * mm});
            skLineSegment(sketch, "E7.8.2.9", {"start": v(-40.6, 84) * mm, "end": v(-40.6, 62) * mm});
            skArc(sketch, "E7.8.2.10", {"start": v(-40.6, 84) * mm, "mid": v(-40.9, 84.7) * mm, "end": v(-41.6, 85) * mm});
            skArc(sketch, "E7.8.2.11", {"start": v(-41.6, 61) * mm, "mid": v(-40.9, 61.3) * mm, "end": v(-40.6, 62) * mm});
            skArc(sketch, "E7.8.2.12", {"start": v(-60.6, 62) * mm, "mid": v(-60.3, 61.3) * mm, "end": v(-59.6, 61) * mm});
            skArc(sketch, "E7.8.2.13", {"start": v(-59.6, 85) * mm, "mid": v(-60.3, 84.7) * mm, "end": v(-60.6, 84) * mm});
            skLineSegment(sketch, "E7.9.0.0", {"start": v(-18.8, 123) * mm, "end": v(-38.8, 123) * mm, "construction": true});
            skPoint(sketch, "E7.9.0.1", {"position": v(-38.8, 135) * mm});
            skLineSegment(sketch, "E7.9.0.2", {"start": v(-38.8, 134) * mm, "end": v(-38.8, 112) * mm});
            skPoint(sketch, "E7.9.0.3", {"position": v(-18.8, 135) * mm});
            skLineSegment(sketch, "E7.9.0.4", {"start": v(-37.8, 111) * mm, "end": v(-19.8, 111) * mm});
            skPoint(sketch, "E7.9.0.5", {"position": v(-38.8, 111) * mm});
            skPoint(sketch, "E7.9.0.6", {"position": v(-18.8, 111) * mm});
            skCircle(sketch, "E7.9.0.7", {"center": v(-28.8, 123) * mm, "radius": 6.5 * mm});
            skLineSegment(sketch, "E7.9.0.8", {"start": v(-37.8, 135) * mm, "end": v(-19.8, 135) * mm});
            skLineSegment(sketch, "E7.9.0.9", {"start": v(-18.8, 134) * mm, "end": v(-18.8, 112) * mm});
            skArc(sketch, "E7.9.0.10", {"start": v(-18.8, 134) * mm, "mid": v(-19.1, 134.7) * mm, "end": v(-19.8, 135) * mm});
            skArc(sketch, "E7.9.0.11", {"start": v(-19.8, 111) * mm, "mid": v(-19.1, 111.3) * mm, "end": v(-18.8, 112) * mm});
            skArc(sketch, "E7.9.0.12", {"start": v(-38.8, 112) * mm, "mid": v(-38.5, 111.3) * mm, "end": v(-37.8, 111) * mm});
            skArc(sketch, "E7.9.0.13", {"start": v(-37.8, 135) * mm, "mid": v(-38.5, 134.7) * mm, "end": v(-38.8, 134) * mm});
            skLineSegment(sketch, "E7.9.1.0", {"start": v(-18.8, 98) * mm, "end": v(-38.8, 98) * mm, "construction": true});
            skPoint(sketch, "E7.9.1.1", {"position": v(-38.8, 110) * mm});
            skLineSegment(sketch, "E7.9.1.2", {"start": v(-38.8, 109) * mm, "end": v(-38.8, 87) * mm});
            skPoint(sketch, "E7.9.1.3", {"position": v(-18.8, 110) * mm});
            skLineSegment(sketch, "E7.9.1.4", {"start": v(-37.8, 86) * mm, "end": v(-19.8, 86) * mm});
            skPoint(sketch, "E7.9.1.5", {"position": v(-38.8, 86) * mm});
            skPoint(sketch, "E7.9.1.6", {"position": v(-18.8, 86) * mm});
            skCircle(sketch, "E7.9.1.7", {"center": v(-28.8, 98) * mm, "radius": 6.5 * mm});
            skLineSegment(sketch, "E7.9.1.8", {"start": v(-37.8, 110) * mm, "end": v(-19.8, 110) * mm});
            skLineSegment(sketch, "E7.9.1.9", {"start": v(-18.8, 109) * mm, "end": v(-18.8, 87) * mm});
            skArc(sketch, "E7.9.1.10", {"start": v(-18.8, 109) * mm, "mid": v(-19.1, 109.7) * mm, "end": v(-19.8, 110) * mm});
            skArc(sketch, "E7.9.1.11", {"start": v(-19.8, 86) * mm, "mid": v(-19.1, 86.3) * mm, "end": v(-18.8, 87) * mm});
            skArc(sketch, "E7.9.1.12", {"start": v(-38.8, 87) * mm, "mid": v(-38.5, 86.3) * mm, "end": v(-37.8, 86) * mm});
            skArc(sketch, "E7.9.1.13", {"start": v(-37.8, 110) * mm, "mid": v(-38.5, 109.7) * mm, "end": v(-38.8, 109) * mm});
            skLineSegment(sketch, "E7.9.2.0", {"start": v(-18.8, 73) * mm, "end": v(-38.8, 73) * mm, "construction": true});
            skPoint(sketch, "E7.9.2.1", {"position": v(-38.8, 85) * mm});
            skLineSegment(sketch, "E7.9.2.2", {"start": v(-38.8, 84) * mm, "end": v(-38.8, 62) * mm});
            skPoint(sketch, "E7.9.2.3", {"position": v(-18.8, 85) * mm});
            skLineSegment(sketch, "E7.9.2.4", {"start": v(-37.8, 61) * mm, "end": v(-19.8, 61) * mm});
            skPoint(sketch, "E7.9.2.5", {"position": v(-38.8, 61) * mm});
            skPoint(sketch, "E7.9.2.6", {"position": v(-18.8, 61) * mm});
            skCircle(sketch, "E7.9.2.7", {"center": v(-28.8, 73) * mm, "radius": 6.5 * mm});
            skLineSegment(sketch, "E7.9.2.8", {"start": v(-37.8, 85) * mm, "end": v(-19.8, 85) * mm});
            skLineSegment(sketch, "E7.9.2.9", {"start": v(-18.8, 84) * mm, "end": v(-18.8, 62) * mm});
            skArc(sketch, "E7.9.2.10", {"start": v(-18.8, 84) * mm, "mid": v(-19.1, 84.7) * mm, "end": v(-19.8, 85) * mm});
            skArc(sketch, "E7.9.2.11", {"start": v(-19.8, 61) * mm, "mid": v(-19.1, 61.3) * mm, "end": v(-18.8, 62) * mm});
            skArc(sketch, "E7.9.2.12", {"start": v(-38.8, 62) * mm, "mid": v(-38.5, 61.3) * mm, "end": v(-37.8, 61) * mm});
            skArc(sketch, "E7.9.2.13", {"start": v(-37.8, 85) * mm, "mid": v(-38.5, 84.7) * mm, "end": v(-38.8, 84) * mm});
            skLineSegment(sketch, "E7.10.0.0", {"start": v(3, 123) * mm, "end": v(-17, 123) * mm, "construction": true});
            skPoint(sketch, "E7.10.0.1", {"position": v(-17, 135) * mm});
            skLineSegment(sketch, "E7.10.0.2", {"start": v(-17, 134) * mm, "end": v(-17, 112) * mm});
            skPoint(sketch, "E7.10.0.3", {"position": v(3, 135) * mm});
            skLineSegment(sketch, "E7.10.0.4", {"start": v(-16, 111) * mm, "end": v(2, 111) * mm});
            skPoint(sketch, "E7.10.0.5", {"position": v(-17, 111) * mm});
            skPoint(sketch, "E7.10.0.6", {"position": v(3, 111) * mm});
            skCircle(sketch, "E7.10.0.7", {"center": v(-7, 123) * mm, "radius": 6.5 * mm});
            skLineSegment(sketch, "E7.10.0.8", {"start": v(-16, 135) * mm, "end": v(2, 135) * mm});
            skLineSegment(sketch, "E7.10.0.9", {"start": v(3, 134) * mm, "end": v(3, 112) * mm});
            skArc(sketch, "E7.10.0.10", {"start": v(3, 134) * mm, "mid": v(2.7, 134.7) * mm, "end": v(2, 135) * mm});
            skArc(sketch, "E7.10.0.11", {"start": v(2, 111) * mm, "mid": v(2.7, 111.3) * mm, "end": v(3, 112) * mm});
            skArc(sketch, "E7.10.0.12", {"start": v(-17, 112) * mm, "mid": v(-16.7, 111.3) * mm, "end": v(-16, 111) * mm});
            skArc(sketch, "E7.10.0.13", {"start": v(-16, 135) * mm, "mid": v(-16.7, 134.7) * mm, "end": v(-17, 134) * mm});
            skLineSegment(sketch, "E7.10.1.0", {"start": v(3, 98) * mm, "end": v(-17, 98) * mm, "construction": true});
            skPoint(sketch, "E7.10.1.1", {"position": v(-17, 110) * mm});
            skLineSegment(sketch, "E7.10.1.2", {"start": v(-17, 109) * mm, "end": v(-17, 87) * mm});
            skPoint(sketch, "E7.10.1.3", {"position": v(3, 110) * mm});
            skLineSegment(sketch, "E7.10.1.4", {"start": v(-16, 86) * mm, "end": v(2, 86) * mm});
            skPoint(sketch, "E7.10.1.5", {"position": v(-17, 86) * mm});
            skPoint(sketch, "E7.10.1.6", {"position": v(3, 86) * mm});
            skCircle(sketch, "E7.10.1.7", {"center": v(-7, 98) * mm, "radius": 6.5 * mm});
            skLineSegment(sketch, "E7.10.1.8", {"start": v(-16, 110) * mm, "end": v(2, 110) * mm});
            skLineSegment(sketch, "E7.10.1.9", {"start": v(3, 109) * mm, "end": v(3, 87) * mm});
            skArc(sketch, "E7.10.1.10", {"start": v(3, 109) * mm, "mid": v(2.7, 109.7) * mm, "end": v(2, 110) * mm});
            skArc(sketch, "E7.10.1.11", {"start": v(2, 86) * mm, "mid": v(2.7, 86.3) * mm, "end": v(3, 87) * mm});
            skArc(sketch, "E7.10.1.12", {"start": v(-17, 87) * mm, "mid": v(-16.7, 86.3) * mm, "end": v(-16, 86) * mm});
            skArc(sketch, "E7.10.1.13", {"start": v(-16, 110) * mm, "mid": v(-16.7, 109.7) * mm, "end": v(-17, 109) * mm});
            skLineSegment(sketch, "E7.10.2.0", {"start": v(3, 73) * mm, "end": v(-17, 73) * mm, "construction": true});
            skPoint(sketch, "E7.10.2.1", {"position": v(-17, 85) * mm});
            skLineSegment(sketch, "E7.10.2.2", {"start": v(-17, 84) * mm, "end": v(-17, 62) * mm});
            skPoint(sketch, "E7.10.2.3", {"position": v(3, 85) * mm});
            skLineSegment(sketch, "E7.10.2.4", {"start": v(-16, 61) * mm, "end": v(2, 61) * mm});
            skPoint(sketch, "E7.10.2.5", {"position": v(-17, 61) * mm});
            skPoint(sketch, "E7.10.2.6", {"position": v(3, 61) * mm});
            skCircle(sketch, "E7.10.2.7", {"center": v(-7, 73) * mm, "radius": 6.5 * mm});
            skLineSegment(sketch, "E7.10.2.8", {"start": v(-16, 85) * mm, "end": v(2, 85) * mm});
            skLineSegment(sketch, "E7.10.2.9", {"start": v(3, 84) * mm, "end": v(3, 62) * mm});
            skArc(sketch, "E7.10.2.10", {"start": v(3, 84) * mm, "mid": v(2.7, 84.7) * mm, "end": v(2, 85) * mm});
            skArc(sketch, "E7.10.2.11", {"start": v(2, 61) * mm, "mid": v(2.7, 61.3) * mm, "end": v(3, 62) * mm});
            skArc(sketch, "E7.10.2.12", {"start": v(-17, 62) * mm, "mid": v(-16.7, 61.3) * mm, "end": v(-16, 61) * mm});
            skArc(sketch, "E7.10.2.13", {"start": v(-16, 85) * mm, "mid": v(-16.7, 84.7) * mm, "end": v(-17, 84) * mm});
            skLineSegment(sketch, "E7.11.0.0", {"start": v(24.8, 123) * mm, "end": v(4.8, 123) * mm, "construction": true});
            skPoint(sketch, "E7.11.0.1", {"position": v(4.8, 135) * mm});
            skLineSegment(sketch, "E7.11.0.2", {"start": v(4.8, 134) * mm, "end": v(4.8, 112) * mm});
            skPoint(sketch, "E7.11.0.3", {"position": v(24.8, 135) * mm});
            skLineSegment(sketch, "E7.11.0.4", {"start": v(5.8, 111) * mm, "end": v(23.8, 111) * mm});
            skPoint(sketch, "E7.11.0.5", {"position": v(4.8, 111) * mm});
            skPoint(sketch, "E7.11.0.6", {"position": v(24.8, 111) * mm});
            skCircle(sketch, "E7.11.0.7", {"center": v(14.8, 123) * mm, "radius": 6.5 * mm});
            skLineSegment(sketch, "E7.11.0.8", {"start": v(5.8, 135) * mm, "end": v(23.8, 135) * mm});
            skLineSegment(sketch, "E7.11.0.9", {"start": v(24.8, 134) * mm, "end": v(24.8, 112) * mm});
            skArc(sketch, "E7.11.0.10", {"start": v(24.8, 134) * mm, "mid": v(24.5, 134.7) * mm, "end": v(23.8, 135) * mm});
            skArc(sketch, "E7.11.0.11", {"start": v(23.8, 111) * mm, "mid": v(24.5, 111.3) * mm, "end": v(24.8, 112) * mm});
            skArc(sketch, "E7.11.0.12", {"start": v(4.8, 112) * mm, "mid": v(5.1, 111.3) * mm, "end": v(5.8, 111) * mm});
            skArc(sketch, "E7.11.0.13", {"start": v(5.8, 135) * mm, "mid": v(5.1, 134.7) * mm, "end": v(4.8, 134) * mm});
            skLineSegment(sketch, "E7.11.1.0", {"start": v(24.8, 98) * mm, "end": v(4.8, 98) * mm, "construction": true});
            skPoint(sketch, "E7.11.1.1", {"position": v(4.8, 110) * mm});
            skLineSegment(sketch, "E7.11.1.2", {"start": v(4.8, 109) * mm, "end": v(4.8, 87) * mm});
            skPoint(sketch, "E7.11.1.3", {"position": v(24.8, 110) * mm});
            skLineSegment(sketch, "E7.11.1.4", {"start": v(5.8, 86) * mm, "end": v(23.8, 86) * mm});
            skPoint(sketch, "E7.11.1.5", {"position": v(4.8, 86) * mm});
            skPoint(sketch, "E7.11.1.6", {"position": v(24.8, 86) * mm});
            skCircle(sketch, "E7.11.1.7", {"center": v(14.8, 98) * mm, "radius": 6.5 * mm});
            skLineSegment(sketch, "E7.11.1.8", {"start": v(5.8, 110) * mm, "end": v(23.8, 110) * mm});
            skLineSegment(sketch, "E7.11.1.9", {"start": v(24.8, 109) * mm, "end": v(24.8, 87) * mm});
            skArc(sketch, "E7.11.1.10", {"start": v(24.8, 109) * mm, "mid": v(24.5, 109.7) * mm, "end": v(23.8, 110) * mm});
            skArc(sketch, "E7.11.1.11", {"start": v(23.8, 86) * mm, "mid": v(24.5, 86.3) * mm, "end": v(24.8, 87) * mm});
            skArc(sketch, "E7.11.1.12", {"start": v(4.8, 87) * mm, "mid": v(5.1, 86.3) * mm, "end": v(5.8, 86) * mm});
            skArc(sketch, "E7.11.1.13", {"start": v(5.8, 110) * mm, "mid": v(5.1, 109.7) * mm, "end": v(4.8, 109) * mm});
            skLineSegment(sketch, "E7.11.2.0", {"start": v(24.8, 73) * mm, "end": v(4.8, 73) * mm, "construction": true});
            skPoint(sketch, "E7.11.2.1", {"position": v(4.8, 85) * mm});
            skLineSegment(sketch, "E7.11.2.2", {"start": v(4.8, 84) * mm, "end": v(4.8, 62) * mm});
            skPoint(sketch, "E7.11.2.3", {"position": v(24.8, 85) * mm});
            skLineSegment(sketch, "E7.11.2.4", {"start": v(5.8, 61) * mm, "end": v(23.8, 61) * mm});
            skPoint(sketch, "E7.11.2.5", {"position": v(4.8, 61) * mm});
            skPoint(sketch, "E7.11.2.6", {"position": v(24.8, 61) * mm});
            skCircle(sketch, "E7.11.2.7", {"center": v(14.8, 73) * mm, "radius": 6.5 * mm});
            skLineSegment(sketch, "E7.11.2.8", {"start": v(5.8, 85) * mm, "end": v(23.8, 85) * mm});
            skLineSegment(sketch, "E7.11.2.9", {"start": v(24.8, 84) * mm, "end": v(24.8, 62) * mm});
            skArc(sketch, "E7.11.2.10", {"start": v(24.8, 84) * mm, "mid": v(24.5, 84.7) * mm, "end": v(23.8, 85) * mm});
            skArc(sketch, "E7.11.2.11", {"start": v(23.8, 61) * mm, "mid": v(24.5, 61.3) * mm, "end": v(24.8, 62) * mm});
            skArc(sketch, "E7.11.2.12", {"start": v(4.8, 62) * mm, "mid": v(5.1, 61.3) * mm, "end": v(5.8, 61) * mm});
            skArc(sketch, "E7.11.2.13", {"start": v(5.8, 85) * mm, "mid": v(5.1, 84.7) * mm, "end": v(4.8, 84) * mm});
            skLineSegment(sketch, "E7.12.0.0", {"start": v(46.6, 123) * mm, "end": v(26.6, 123) * mm, "construction": true});
            skPoint(sketch, "E7.12.0.1", {"position": v(26.6, 135) * mm});
            skLineSegment(sketch, "E7.12.0.2", {"start": v(26.6, 134) * mm, "end": v(26.6, 112) * mm});
            skPoint(sketch, "E7.12.0.3", {"position": v(46.6, 135) * mm});
            skLineSegment(sketch, "E7.12.0.4", {"start": v(27.6, 111) * mm, "end": v(45.6, 111) * mm});
            skPoint(sketch, "E7.12.0.5", {"position": v(26.6, 111) * mm});
            skPoint(sketch, "E7.12.0.6", {"position": v(46.6, 111) * mm});
            skCircle(sketch, "E7.12.0.7", {"center": v(36.6, 123) * mm, "radius": 6.5 * mm});
            skLineSegment(sketch, "E7.12.0.8", {"start": v(27.6, 135) * mm, "end": v(45.6, 135) * mm});
            skLineSegment(sketch, "E7.12.0.9", {"start": v(46.6, 134) * mm, "end": v(46.6, 112) * mm});
            skArc(sketch, "E7.12.0.10", {"start": v(46.6, 134) * mm, "mid": v(46.3, 134.7) * mm, "end": v(45.6, 135) * mm});
            skArc(sketch, "E7.12.0.11", {"start": v(45.6, 111) * mm, "mid": v(46.3, 111.3) * mm, "end": v(46.6, 112) * mm});
            skArc(sketch, "E7.12.0.12", {"start": v(26.6, 112) * mm, "mid": v(26.9, 111.3) * mm, "end": v(27.6, 111) * mm});
            skArc(sketch, "E7.12.0.13", {"start": v(27.6, 135) * mm, "mid": v(26.9, 134.7) * mm, "end": v(26.6, 134) * mm});
            skLineSegment(sketch, "E7.12.1.0", {"start": v(46.6, 98) * mm, "end": v(26.6, 98) * mm, "construction": true});
            skPoint(sketch, "E7.12.1.1", {"position": v(26.6, 110) * mm});
            skLineSegment(sketch, "E7.12.1.2", {"start": v(26.6, 109) * mm, "end": v(26.6, 87) * mm});
            skPoint(sketch, "E7.12.1.3", {"position": v(46.6, 110) * mm});
            skLineSegment(sketch, "E7.12.1.4", {"start": v(27.6, 86) * mm, "end": v(45.6, 86) * mm});
            skPoint(sketch, "E7.12.1.5", {"position": v(26.6, 86) * mm});
            skPoint(sketch, "E7.12.1.6", {"position": v(46.6, 86) * mm});
            skCircle(sketch, "E7.12.1.7", {"center": v(36.6, 98) * mm, "radius": 6.5 * mm});
            skLineSegment(sketch, "E7.12.1.8", {"start": v(27.6, 110) * mm, "end": v(45.6, 110) * mm});
            skLineSegment(sketch, "E7.12.1.9", {"start": v(46.6, 109) * mm, "end": v(46.6, 87) * mm});
            skArc(sketch, "E7.12.1.10", {"start": v(46.6, 109) * mm, "mid": v(46.3, 109.7) * mm, "end": v(45.6, 110) * mm});
            skArc(sketch, "E7.12.1.11", {"start": v(45.6, 86) * mm, "mid": v(46.3, 86.3) * mm, "end": v(46.6, 87) * mm});
            skArc(sketch, "E7.12.1.12", {"start": v(26.6, 87) * mm, "mid": v(26.9, 86.3) * mm, "end": v(27.6, 86) * mm});
            skArc(sketch, "E7.12.1.13", {"start": v(27.6, 110) * mm, "mid": v(26.9, 109.7) * mm, "end": v(26.6, 109) * mm});
            skLineSegment(sketch, "E7.12.2.0", {"start": v(46.6, 73) * mm, "end": v(26.6, 73) * mm, "construction": true});
            skPoint(sketch, "E7.12.2.1", {"position": v(26.6, 85) * mm});
            skLineSegment(sketch, "E7.12.2.2", {"start": v(26.6, 84) * mm, "end": v(26.6, 62) * mm});
            skPoint(sketch, "E7.12.2.3", {"position": v(46.6, 85) * mm});
            skLineSegment(sketch, "E7.12.2.4", {"start": v(27.6, 61) * mm, "end": v(45.6, 61) * mm});
            skPoint(sketch, "E7.12.2.5", {"position": v(26.6, 61) * mm});
            skPoint(sketch, "E7.12.2.6", {"position": v(46.6, 61) * mm});
            skCircle(sketch, "E7.12.2.7", {"center": v(36.6, 73) * mm, "radius": 6.5 * mm});
            skLineSegment(sketch, "E7.12.2.8", {"start": v(27.6, 85) * mm, "end": v(45.6, 85) * mm});
            skLineSegment(sketch, "E7.12.2.9", {"start": v(46.6, 84) * mm, "end": v(46.6, 62) * mm});
            skArc(sketch, "E7.12.2.10", {"start": v(46.6, 84) * mm, "mid": v(46.3, 84.7) * mm, "end": v(45.6, 85) * mm});
            skArc(sketch, "E7.12.2.11", {"start": v(45.6, 61) * mm, "mid": v(46.3, 61.3) * mm, "end": v(46.6, 62) * mm});
            skArc(sketch, "E7.12.2.12", {"start": v(26.6, 62) * mm, "mid": v(26.9, 61.3) * mm, "end": v(27.6, 61) * mm});
            skArc(sketch, "E7.12.2.13", {"start": v(27.6, 85) * mm, "mid": v(26.9, 84.7) * mm, "end": v(26.6, 84) * mm});
            skLineSegment(sketch, "E7.13.0.0", {"start": v(68.4, 123) * mm, "end": v(48.4, 123) * mm, "construction": true});
            skPoint(sketch, "E7.13.0.1", {"position": v(48.4, 135) * mm});
            skLineSegment(sketch, "E7.13.0.2", {"start": v(48.4, 134) * mm, "end": v(48.4, 112) * mm});
            skPoint(sketch, "E7.13.0.3", {"position": v(68.4, 135) * mm});
            skLineSegment(sketch, "E7.13.0.4", {"start": v(49.4, 111) * mm, "end": v(67.4, 111) * mm});
            skPoint(sketch, "E7.13.0.5", {"position": v(48.4, 111) * mm});
            skPoint(sketch, "E7.13.0.6", {"position": v(68.4, 111) * mm});
            skCircle(sketch, "E7.13.0.7", {"center": v(58.4, 123) * mm, "radius": 6.5 * mm});
            skLineSegment(sketch, "E7.13.0.8", {"start": v(49.4, 135) * mm, "end": v(67.4, 135) * mm});
            skLineSegment(sketch, "E7.13.0.9", {"start": v(68.4, 134) * mm, "end": v(68.4, 112) * mm});
            skArc(sketch, "E7.13.0.10", {"start": v(68.4, 134) * mm, "mid": v(68.1, 134.7) * mm, "end": v(67.4, 135) * mm});
            skArc(sketch, "E7.13.0.11", {"start": v(67.4, 111) * mm, "mid": v(68.1, 111.3) * mm, "end": v(68.4, 112) * mm});
            skArc(sketch, "E7.13.0.12", {"start": v(48.4, 112) * mm, "mid": v(48.7, 111.3) * mm, "end": v(49.4, 111) * mm});
            skArc(sketch, "E7.13.0.13", {"start": v(49.4, 135) * mm, "mid": v(48.7, 134.7) * mm, "end": v(48.4, 134) * mm});
            skLineSegment(sketch, "E7.13.1.0", {"start": v(68.4, 98) * mm, "end": v(48.4, 98) * mm, "construction": true});
            skPoint(sketch, "E7.13.1.1", {"position": v(48.4, 110) * mm});
            skLineSegment(sketch, "E7.13.1.2", {"start": v(48.4, 109) * mm, "end": v(48.4, 87) * mm});
            skPoint(sketch, "E7.13.1.3", {"position": v(68.4, 110) * mm});
            skLineSegment(sketch, "E7.13.1.4", {"start": v(49.4, 86) * mm, "end": v(67.4, 86) * mm});
            skPoint(sketch, "E7.13.1.5", {"position": v(48.4, 86) * mm});
            skPoint(sketch, "E7.13.1.6", {"position": v(68.4, 86) * mm});
            skCircle(sketch, "E7.13.1.7", {"center": v(58.4, 98) * mm, "radius": 6.5 * mm});
            skLineSegment(sketch, "E7.13.1.8", {"start": v(49.4, 110) * mm, "end": v(67.4, 110) * mm});
            skLineSegment(sketch, "E7.13.1.9", {"start": v(68.4, 109) * mm, "end": v(68.4, 87) * mm});
            skArc(sketch, "E7.13.1.10", {"start": v(68.4, 109) * mm, "mid": v(68.1, 109.7) * mm, "end": v(67.4, 110) * mm});
            skArc(sketch, "E7.13.1.11", {"start": v(67.4, 86) * mm, "mid": v(68.1, 86.3) * mm, "end": v(68.4, 87) * mm});
            skArc(sketch, "E7.13.1.12", {"start": v(48.4, 87) * mm, "mid": v(48.7, 86.3) * mm, "end": v(49.4, 86) * mm});
            skArc(sketch, "E7.13.1.13", {"start": v(49.4, 110) * mm, "mid": v(48.7, 109.7) * mm, "end": v(48.4, 109) * mm});
            skLineSegment(sketch, "E7.13.2.0", {"start": v(68.4, 73) * mm, "end": v(48.4, 73) * mm, "construction": true});
            skPoint(sketch, "E7.13.2.1", {"position": v(48.4, 85) * mm});
            skLineSegment(sketch, "E7.13.2.2", {"start": v(48.4, 84) * mm, "end": v(48.4, 62) * mm});
            skPoint(sketch, "E7.13.2.3", {"position": v(68.4, 85) * mm});
            skLineSegment(sketch, "E7.13.2.4", {"start": v(49.4, 61) * mm, "end": v(67.4, 61) * mm});
            skPoint(sketch, "E7.13.2.5", {"position": v(48.4, 61) * mm});
            skPoint(sketch, "E7.13.2.6", {"position": v(68.4, 61) * mm});
            skCircle(sketch, "E7.13.2.7", {"center": v(58.4, 73) * mm, "radius": 6.5 * mm});
            skLineSegment(sketch, "E7.13.2.8", {"start": v(49.4, 85) * mm, "end": v(67.4, 85) * mm});
            skLineSegment(sketch, "E7.13.2.9", {"start": v(68.4, 84) * mm, "end": v(68.4, 62) * mm});
            skArc(sketch, "E7.13.2.10", {"start": v(68.4, 84) * mm, "mid": v(68.1, 84.7) * mm, "end": v(67.4, 85) * mm});
            skArc(sketch, "E7.13.2.11", {"start": v(67.4, 61) * mm, "mid": v(68.1, 61.3) * mm, "end": v(68.4, 62) * mm});
            skArc(sketch, "E7.13.2.12", {"start": v(48.4, 62) * mm, "mid": v(48.7, 61.3) * mm, "end": v(49.4, 61) * mm});
            skArc(sketch, "E7.13.2.13", {"start": v(49.4, 85) * mm, "mid": v(48.7, 84.7) * mm, "end": v(48.4, 84) * mm});
            skLineSegment(sketch, "E7.14.0.0", {"start": v(90.2, 123) * mm, "end": v(70.2, 123) * mm, "construction": true});
            skPoint(sketch, "E7.14.0.1", {"position": v(70.2, 135) * mm});
            skLineSegment(sketch, "E7.14.0.2", {"start": v(70.2, 134) * mm, "end": v(70.2, 112) * mm});
            skPoint(sketch, "E7.14.0.3", {"position": v(90.2, 135) * mm});
            skLineSegment(sketch, "E7.14.0.4", {"start": v(71.2, 111) * mm, "end": v(89.2, 111) * mm});
            skPoint(sketch, "E7.14.0.5", {"position": v(70.2, 111) * mm});
            skPoint(sketch, "E7.14.0.6", {"position": v(90.2, 111) * mm});
            skCircle(sketch, "E7.14.0.7", {"center": v(80.2, 123) * mm, "radius": 6.5 * mm});
            skLineSegment(sketch, "E7.14.0.8", {"start": v(71.2, 135) * mm, "end": v(89.2, 135) * mm});
            skLineSegment(sketch, "E7.14.0.9", {"start": v(90.2, 134) * mm, "end": v(90.2, 112) * mm});
            skArc(sketch, "E7.14.0.10", {"start": v(90.2, 134) * mm, "mid": v(89.9, 134.7) * mm, "end": v(89.2, 135) * mm});
            skArc(sketch, "E7.14.0.11", {"start": v(89.2, 111) * mm, "mid": v(89.9, 111.3) * mm, "end": v(90.2, 112) * mm});
            skArc(sketch, "E7.14.0.12", {"start": v(70.2, 112) * mm, "mid": v(70.5, 111.3) * mm, "end": v(71.2, 111) * mm});
            skArc(sketch, "E7.14.0.13", {"start": v(71.2, 135) * mm, "mid": v(70.5, 134.7) * mm, "end": v(70.2, 134) * mm});
            skLineSegment(sketch, "E7.14.1.0", {"start": v(90.2, 98) * mm, "end": v(70.2, 98) * mm, "construction": true});
            skPoint(sketch, "E7.14.1.1", {"position": v(70.2, 110) * mm});
            skLineSegment(sketch, "E7.14.1.2", {"start": v(70.2, 109) * mm, "end": v(70.2, 87) * mm});
            skPoint(sketch, "E7.14.1.3", {"position": v(90.2, 110) * mm});
            skLineSegment(sketch, "E7.14.1.4", {"start": v(71.2, 86) * mm, "end": v(89.2, 86) * mm});
            skPoint(sketch, "E7.14.1.5", {"position": v(70.2, 86) * mm});
            skPoint(sketch, "E7.14.1.6", {"position": v(90.2, 86) * mm});
            skCircle(sketch, "E7.14.1.7", {"center": v(80.2, 98) * mm, "radius": 6.5 * mm});
            skLineSegment(sketch, "E7.14.1.8", {"start": v(71.2, 110) * mm, "end": v(89.2, 110) * mm});
            skLineSegment(sketch, "E7.14.1.9", {"start": v(90.2, 109) * mm, "end": v(90.2, 87) * mm});
            skArc(sketch, "E7.14.1.10", {"start": v(90.2, 109) * mm, "mid": v(89.9, 109.7) * mm, "end": v(89.2, 110) * mm});
            skArc(sketch, "E7.14.1.11", {"start": v(89.2, 86) * mm, "mid": v(89.9, 86.3) * mm, "end": v(90.2, 87) * mm});
            skArc(sketch, "E7.14.1.12", {"start": v(70.2, 87) * mm, "mid": v(70.5, 86.3) * mm, "end": v(71.2, 86) * mm});
            skArc(sketch, "E7.14.1.13", {"start": v(71.2, 110) * mm, "mid": v(70.5, 109.7) * mm, "end": v(70.2, 109) * mm});
            skLineSegment(sketch, "E7.14.2.0", {"start": v(90.2, 73) * mm, "end": v(70.2, 73) * mm, "construction": true});
            skPoint(sketch, "E7.14.2.1", {"position": v(70.2, 85) * mm});
            skLineSegment(sketch, "E7.14.2.2", {"start": v(70.2, 84) * mm, "end": v(70.2, 62) * mm});
            skPoint(sketch, "E7.14.2.3", {"position": v(90.2, 85) * mm});
            skLineSegment(sketch, "E7.14.2.4", {"start": v(71.2, 61) * mm, "end": v(89.2, 61) * mm});
            skPoint(sketch, "E7.14.2.5", {"position": v(70.2, 61) * mm});
            skPoint(sketch, "E7.14.2.6", {"position": v(90.2, 61) * mm});
            skCircle(sketch, "E7.14.2.7", {"center": v(80.2, 73) * mm, "radius": 6.5 * mm});
            skLineSegment(sketch, "E7.14.2.8", {"start": v(71.2, 85) * mm, "end": v(89.2, 85) * mm});
            skLineSegment(sketch, "E7.14.2.9", {"start": v(90.2, 84) * mm, "end": v(90.2, 62) * mm});
            skArc(sketch, "E7.14.2.10", {"start": v(90.2, 84) * mm, "mid": v(89.9, 84.7) * mm, "end": v(89.2, 85) * mm});
            skArc(sketch, "E7.14.2.11", {"start": v(89.2, 61) * mm, "mid": v(89.9, 61.3) * mm, "end": v(90.2, 62) * mm});
            skArc(sketch, "E7.14.2.12", {"start": v(70.2, 62) * mm, "mid": v(70.5, 61.3) * mm, "end": v(71.2, 61) * mm});
            skArc(sketch, "E7.14.2.13", {"start": v(71.2, 85) * mm, "mid": v(70.5, 84.7) * mm, "end": v(70.2, 84) * mm});
            skLineSegment(sketch, "E7.15.0.0", {"start": v(112, 123) * mm, "end": v(92, 123) * mm, "construction": true});
            skPoint(sketch, "E7.15.0.1", {"position": v(92, 135) * mm});
            skLineSegment(sketch, "E7.15.0.2", {"start": v(92, 134) * mm, "end": v(92, 112) * mm});
            skPoint(sketch, "E7.15.0.3", {"position": v(112, 135) * mm});
            skLineSegment(sketch, "E7.15.0.4", {"start": v(93, 111) * mm, "end": v(111, 111) * mm});
            skPoint(sketch, "E7.15.0.5", {"position": v(92, 111) * mm});
            skPoint(sketch, "E7.15.0.6", {"position": v(112, 111) * mm});
            skCircle(sketch, "E7.15.0.7", {"center": v(102, 123) * mm, "radius": 6.5 * mm});
            skLineSegment(sketch, "E7.15.0.8", {"start": v(93, 135) * mm, "end": v(111, 135) * mm});
            skLineSegment(sketch, "E7.15.0.9", {"start": v(112, 134) * mm, "end": v(112, 112) * mm});
            skArc(sketch, "E7.15.0.10", {"start": v(112, 134) * mm, "mid": v(111.7, 134.7) * mm, "end": v(111, 135) * mm});
            skArc(sketch, "E7.15.0.11", {"start": v(111, 111) * mm, "mid": v(111.7, 111.3) * mm, "end": v(112, 112) * mm});
            skArc(sketch, "E7.15.0.12", {"start": v(92, 112) * mm, "mid": v(92.3, 111.3) * mm, "end": v(93, 111) * mm});
            skArc(sketch, "E7.15.0.13", {"start": v(93, 135) * mm, "mid": v(92.3, 134.7) * mm, "end": v(92, 134) * mm});
            skLineSegment(sketch, "E7.15.1.0", {"start": v(112, 98) * mm, "end": v(92, 98) * mm, "construction": true});
            skPoint(sketch, "E7.15.1.1", {"position": v(92, 110) * mm});
            skLineSegment(sketch, "E7.15.1.2", {"start": v(92, 109) * mm, "end": v(92, 87) * mm});
            skPoint(sketch, "E7.15.1.3", {"position": v(112, 110) * mm});
            skLineSegment(sketch, "E7.15.1.4", {"start": v(93, 86) * mm, "end": v(111, 86) * mm});
            skPoint(sketch, "E7.15.1.5", {"position": v(92, 86) * mm});
            skPoint(sketch, "E7.15.1.6", {"position": v(112, 86) * mm});
            skCircle(sketch, "E7.15.1.7", {"center": v(102, 98) * mm, "radius": 6.5 * mm});
            skLineSegment(sketch, "E7.15.1.8", {"start": v(93, 110) * mm, "end": v(111, 110) * mm});
            skLineSegment(sketch, "E7.15.1.9", {"start": v(112, 109) * mm, "end": v(112, 87) * mm});
            skArc(sketch, "E7.15.1.10", {"start": v(112, 109) * mm, "mid": v(111.7, 109.7) * mm, "end": v(111, 110) * mm});
            skArc(sketch, "E7.15.1.11", {"start": v(111, 86) * mm, "mid": v(111.7, 86.3) * mm, "end": v(112, 87) * mm});
            skArc(sketch, "E7.15.1.12", {"start": v(92, 87) * mm, "mid": v(92.3, 86.3) * mm, "end": v(93, 86) * mm});
            skArc(sketch, "E7.15.1.13", {"start": v(93, 110) * mm, "mid": v(92.3, 109.7) * mm, "end": v(92, 109) * mm});
            skLineSegment(sketch, "E7.15.2.0", {"start": v(112, 73) * mm, "end": v(92, 73) * mm, "construction": true});
            skPoint(sketch, "E7.15.2.1", {"position": v(92, 85) * mm});
            skLineSegment(sketch, "E7.15.2.2", {"start": v(92, 84) * mm, "end": v(92, 62) * mm});
            skPoint(sketch, "E7.15.2.3", {"position": v(112, 85) * mm});
            skLineSegment(sketch, "E7.15.2.4", {"start": v(93, 61) * mm, "end": v(111, 61) * mm});
            skPoint(sketch, "E7.15.2.5", {"position": v(92, 61) * mm});
            skPoint(sketch, "E7.15.2.6", {"position": v(112, 61) * mm});
            skCircle(sketch, "E7.15.2.7", {"center": v(102, 73) * mm, "radius": 6.5 * mm});
            skLineSegment(sketch, "E7.15.2.8", {"start": v(93, 85) * mm, "end": v(111, 85) * mm});
            skLineSegment(sketch, "E7.15.2.9", {"start": v(112, 84) * mm, "end": v(112, 62) * mm});
            skArc(sketch, "E7.15.2.10", {"start": v(112, 84) * mm, "mid": v(111.7, 84.7) * mm, "end": v(111, 85) * mm});
            skArc(sketch, "E7.15.2.11", {"start": v(111, 61) * mm, "mid": v(111.7, 61.3) * mm, "end": v(112, 62) * mm});
            skArc(sketch, "E7.15.2.12", {"start": v(92, 62) * mm, "mid": v(92.3, 61.3) * mm, "end": v(93, 61) * mm});
            skArc(sketch, "E7.15.2.13", {"start": v(93, 85) * mm, "mid": v(92.3, 84.7) * mm, "end": v(92, 84) * mm});
            skLineSegment(sketch, "E7.16.0.0", {"start": v(133.8, 123) * mm, "end": v(113.8, 123) * mm, "construction": true});
            skPoint(sketch, "E7.16.0.1", {"position": v(113.8, 135) * mm});
            skLineSegment(sketch, "E7.16.0.2", {"start": v(113.8, 134) * mm, "end": v(113.8, 112) * mm});
            skPoint(sketch, "E7.16.0.3", {"position": v(133.8, 135) * mm});
            skLineSegment(sketch, "E7.16.0.4", {"start": v(114.8, 111) * mm, "end": v(132.8, 111) * mm});
            skPoint(sketch, "E7.16.0.5", {"position": v(113.8, 111) * mm});
            skPoint(sketch, "E7.16.0.6", {"position": v(133.8, 111) * mm});
            skCircle(sketch, "E7.16.0.7", {"center": v(123.8, 123) * mm, "radius": 6.5 * mm});
            skLineSegment(sketch, "E7.16.0.8", {"start": v(114.8, 135) * mm, "end": v(132.8, 135) * mm});
            skLineSegment(sketch, "E7.16.0.9", {"start": v(133.8, 134) * mm, "end": v(133.8, 112) * mm});
            skArc(sketch, "E7.16.0.10", {"start": v(133.8, 134) * mm, "mid": v(133.5, 134.7) * mm, "end": v(132.8, 135) * mm});
            skArc(sketch, "E7.16.0.11", {"start": v(132.8, 111) * mm, "mid": v(133.5, 111.3) * mm, "end": v(133.8, 112) * mm});
            skArc(sketch, "E7.16.0.12", {"start": v(113.8, 112) * mm, "mid": v(114.1, 111.3) * mm, "end": v(114.8, 111) * mm});
            skArc(sketch, "E7.16.0.13", {"start": v(114.8, 135) * mm, "mid": v(114.1, 134.7) * mm, "end": v(113.8, 134) * mm});
            skLineSegment(sketch, "E7.16.1.0", {"start": v(133.8, 98) * mm, "end": v(113.8, 98) * mm, "construction": true});
            skPoint(sketch, "E7.16.1.1", {"position": v(113.8, 110) * mm});
            skLineSegment(sketch, "E7.16.1.2", {"start": v(113.8, 109) * mm, "end": v(113.8, 87) * mm});
            skPoint(sketch, "E7.16.1.3", {"position": v(133.8, 110) * mm});
            skLineSegment(sketch, "E7.16.1.4", {"start": v(114.8, 86) * mm, "end": v(132.8, 86) * mm});
            skPoint(sketch, "E7.16.1.5", {"position": v(113.8, 86) * mm});
            skPoint(sketch, "E7.16.1.6", {"position": v(133.8, 86) * mm});
            skCircle(sketch, "E7.16.1.7", {"center": v(123.8, 98) * mm, "radius": 6.5 * mm});
            skLineSegment(sketch, "E7.16.1.8", {"start": v(114.8, 110) * mm, "end": v(132.8, 110) * mm});
            skLineSegment(sketch, "E7.16.1.9", {"start": v(133.8, 109) * mm, "end": v(133.8, 87) * mm});
            skArc(sketch, "E7.16.1.10", {"start": v(133.8, 109) * mm, "mid": v(133.5, 109.7) * mm, "end": v(132.8, 110) * mm});
            skArc(sketch, "E7.16.1.11", {"start": v(132.8, 86) * mm, "mid": v(133.5, 86.3) * mm, "end": v(133.8, 87) * mm});
            skArc(sketch, "E7.16.1.12", {"start": v(113.8, 87) * mm, "mid": v(114.1, 86.3) * mm, "end": v(114.8, 86) * mm});
            skArc(sketch, "E7.16.1.13", {"start": v(114.8, 110) * mm, "mid": v(114.1, 109.7) * mm, "end": v(113.8, 109) * mm});
            skLineSegment(sketch, "E7.16.2.0", {"start": v(133.8, 73) * mm, "end": v(113.8, 73) * mm, "construction": true});
            skPoint(sketch, "E7.16.2.1", {"position": v(113.8, 85) * mm});
            skLineSegment(sketch, "E7.16.2.2", {"start": v(113.8, 84) * mm, "end": v(113.8, 62) * mm});
            skPoint(sketch, "E7.16.2.3", {"position": v(133.8, 85) * mm});
            skLineSegment(sketch, "E7.16.2.4", {"start": v(114.8, 61) * mm, "end": v(132.8, 61) * mm});
            skPoint(sketch, "E7.16.2.5", {"position": v(113.8, 61) * mm});
            skPoint(sketch, "E7.16.2.6", {"position": v(133.8, 61) * mm});
            skCircle(sketch, "E7.16.2.7", {"center": v(123.8, 73) * mm, "radius": 6.5 * mm});
            skLineSegment(sketch, "E7.16.2.8", {"start": v(114.8, 85) * mm, "end": v(132.8, 85) * mm});
            skLineSegment(sketch, "E7.16.2.9", {"start": v(133.8, 84) * mm, "end": v(133.8, 62) * mm});
            skArc(sketch, "E7.16.2.10", {"start": v(133.8, 84) * mm, "mid": v(133.5, 84.7) * mm, "end": v(132.8, 85) * mm});
            skArc(sketch, "E7.16.2.11", {"start": v(132.8, 61) * mm, "mid": v(133.5, 61.3) * mm, "end": v(133.8, 62) * mm});
            skArc(sketch, "E7.16.2.12", {"start": v(113.8, 62) * mm, "mid": v(114.1, 61.3) * mm, "end": v(114.8, 61) * mm});
            skArc(sketch, "E7.16.2.13", {"start": v(114.8, 85) * mm, "mid": v(114.1, 84.7) * mm, "end": v(113.8, 84) * mm});
            skLineSegment(sketch, "E7.17.0.0", {"start": v(155.6, 123) * mm, "end": v(135.6, 123) * mm, "construction": true});
            skPoint(sketch, "E7.17.0.1", {"position": v(135.6, 135) * mm});
            skLineSegment(sketch, "E7.17.0.2", {"start": v(135.6, 134) * mm, "end": v(135.6, 112) * mm});
            skPoint(sketch, "E7.17.0.3", {"position": v(155.6, 135) * mm});
            skLineSegment(sketch, "E7.17.0.4", {"start": v(136.6, 111) * mm, "end": v(154.6, 111) * mm});
            skPoint(sketch, "E7.17.0.5", {"position": v(135.6, 111) * mm});
            skPoint(sketch, "E7.17.0.6", {"position": v(155.6, 111) * mm});
            skCircle(sketch, "E7.17.0.7", {"center": v(145.6, 123) * mm, "radius": 6.5 * mm});
            skLineSegment(sketch, "E7.17.0.8", {"start": v(136.6, 135) * mm, "end": v(154.6, 135) * mm});
            skLineSegment(sketch, "E7.17.0.9", {"start": v(155.6, 134) * mm, "end": v(155.6, 112) * mm});
            skArc(sketch, "E7.17.0.10", {"start": v(155.6, 134) * mm, "mid": v(155.3, 134.7) * mm, "end": v(154.6, 135) * mm});
            skArc(sketch, "E7.17.0.11", {"start": v(154.6, 111) * mm, "mid": v(155.3, 111.3) * mm, "end": v(155.6, 112) * mm});
            skArc(sketch, "E7.17.0.12", {"start": v(135.6, 112) * mm, "mid": v(135.9, 111.3) * mm, "end": v(136.6, 111) * mm});
            skArc(sketch, "E7.17.0.13", {"start": v(136.6, 135) * mm, "mid": v(135.9, 134.7) * mm, "end": v(135.6, 134) * mm});
            skLineSegment(sketch, "E7.17.1.0", {"start": v(155.6, 98) * mm, "end": v(135.6, 98) * mm, "construction": true});
            skPoint(sketch, "E7.17.1.1", {"position": v(135.6, 110) * mm});
            skLineSegment(sketch, "E7.17.1.2", {"start": v(135.6, 109) * mm, "end": v(135.6, 87) * mm});
            skPoint(sketch, "E7.17.1.3", {"position": v(155.6, 110) * mm});
            skLineSegment(sketch, "E7.17.1.4", {"start": v(136.6, 86) * mm, "end": v(154.6, 86) * mm});
            skPoint(sketch, "E7.17.1.5", {"position": v(135.6, 86) * mm});
            skPoint(sketch, "E7.17.1.6", {"position": v(155.6, 86) * mm});
            skCircle(sketch, "E7.17.1.7", {"center": v(145.6, 98) * mm, "radius": 6.5 * mm});
            skLineSegment(sketch, "E7.17.1.8", {"start": v(136.6, 110) * mm, "end": v(154.6, 110) * mm});
            skLineSegment(sketch, "E7.17.1.9", {"start": v(155.6, 109) * mm, "end": v(155.6, 87) * mm});
            skArc(sketch, "E7.17.1.10", {"start": v(155.6, 109) * mm, "mid": v(155.3, 109.7) * mm, "end": v(154.6, 110) * mm});
            skArc(sketch, "E7.17.1.11", {"start": v(154.6, 86) * mm, "mid": v(155.3, 86.3) * mm, "end": v(155.6, 87) * mm});
            skArc(sketch, "E7.17.1.12", {"start": v(135.6, 87) * mm, "mid": v(135.9, 86.3) * mm, "end": v(136.6, 86) * mm});
            skArc(sketch, "E7.17.1.13", {"start": v(136.6, 110) * mm, "mid": v(135.9, 109.7) * mm, "end": v(135.6, 109) * mm});
            skLineSegment(sketch, "E7.17.2.0", {"start": v(155.6, 73) * mm, "end": v(135.6, 73) * mm, "construction": true});
            skPoint(sketch, "E7.17.2.1", {"position": v(135.6, 85) * mm});
            skLineSegment(sketch, "E7.17.2.2", {"start": v(135.6, 84) * mm, "end": v(135.6, 62) * mm});
            skPoint(sketch, "E7.17.2.3", {"position": v(155.6, 85) * mm});
            skLineSegment(sketch, "E7.17.2.4", {"start": v(136.6, 61) * mm, "end": v(154.6, 61) * mm});
            skPoint(sketch, "E7.17.2.5", {"position": v(135.6, 61) * mm});
            skPoint(sketch, "E7.17.2.6", {"position": v(155.6, 61) * mm});
            skCircle(sketch, "E7.17.2.7", {"center": v(145.6, 73) * mm, "radius": 6.5 * mm});
            skLineSegment(sketch, "E7.17.2.8", {"start": v(136.6, 85) * mm, "end": v(154.6, 85) * mm});
            skLineSegment(sketch, "E7.17.2.9", {"start": v(155.6, 84) * mm, "end": v(155.6, 62) * mm});
            skArc(sketch, "E7.17.2.10", {"start": v(155.6, 84) * mm, "mid": v(155.3, 84.7) * mm, "end": v(154.6, 85) * mm});
            skArc(sketch, "E7.17.2.11", {"start": v(154.6, 61) * mm, "mid": v(155.3, 61.3) * mm, "end": v(155.6, 62) * mm});
            skArc(sketch, "E7.17.2.12", {"start": v(135.6, 62) * mm, "mid": v(135.9, 61.3) * mm, "end": v(136.6, 61) * mm});
            skArc(sketch, "E7.17.2.13", {"start": v(136.6, 85) * mm, "mid": v(135.9, 84.7) * mm, "end": v(135.6, 84) * mm});
            skLineSegment(sketch, "E7.18.0.0", {"start": v(177.4, 123) * mm, "end": v(157.4, 123) * mm, "construction": true});
            skPoint(sketch, "E7.18.0.1", {"position": v(157.4, 135) * mm});
            skLineSegment(sketch, "E7.18.0.2", {"start": v(157.4, 134) * mm, "end": v(157.4, 112) * mm});
            skPoint(sketch, "E7.18.0.3", {"position": v(177.4, 135) * mm});
            skLineSegment(sketch, "E7.18.0.4", {"start": v(158.4, 111) * mm, "end": v(176.4, 111) * mm});
            skPoint(sketch, "E7.18.0.5", {"position": v(157.4, 111) * mm});
            skPoint(sketch, "E7.18.0.6", {"position": v(177.4, 111) * mm});
            skCircle(sketch, "E7.18.0.7", {"center": v(167.4, 123) * mm, "radius": 6.5 * mm});
            skLineSegment(sketch, "E7.18.0.8", {"start": v(158.4, 135) * mm, "end": v(176.4, 135) * mm});
            skLineSegment(sketch, "E7.18.0.9", {"start": v(177.4, 134) * mm, "end": v(177.4, 112) * mm});
            skArc(sketch, "E7.18.0.10", {"start": v(177.4, 134) * mm, "mid": v(177.1, 134.7) * mm, "end": v(176.4, 135) * mm});
            skArc(sketch, "E7.18.0.11", {"start": v(176.4, 111) * mm, "mid": v(177.1, 111.3) * mm, "end": v(177.4, 112) * mm});
            skArc(sketch, "E7.18.0.12", {"start": v(157.4, 112) * mm, "mid": v(157.7, 111.3) * mm, "end": v(158.4, 111) * mm});
            skArc(sketch, "E7.18.0.13", {"start": v(158.4, 135) * mm, "mid": v(157.7, 134.7) * mm, "end": v(157.4, 134) * mm});
            skLineSegment(sketch, "E7.18.1.0", {"start": v(177.4, 98) * mm, "end": v(157.4, 98) * mm, "construction": true});
            skPoint(sketch, "E7.18.1.1", {"position": v(157.4, 110) * mm});
            skLineSegment(sketch, "E7.18.1.2", {"start": v(157.4, 109) * mm, "end": v(157.4, 87) * mm});
            skPoint(sketch, "E7.18.1.3", {"position": v(177.4, 110) * mm});
            skLineSegment(sketch, "E7.18.1.4", {"start": v(158.4, 86) * mm, "end": v(176.4, 86) * mm});
            skPoint(sketch, "E7.18.1.5", {"position": v(157.4, 86) * mm});
            skPoint(sketch, "E7.18.1.6", {"position": v(177.4, 86) * mm});
            skCircle(sketch, "E7.18.1.7", {"center": v(167.4, 98) * mm, "radius": 6.5 * mm});
            skLineSegment(sketch, "E7.18.1.8", {"start": v(158.4, 110) * mm, "end": v(176.4, 110) * mm});
            skLineSegment(sketch, "E7.18.1.9", {"start": v(177.4, 109) * mm, "end": v(177.4, 87) * mm});
            skArc(sketch, "E7.18.1.10", {"start": v(177.4, 109) * mm, "mid": v(177.1, 109.7) * mm, "end": v(176.4, 110) * mm});
            skArc(sketch, "E7.18.1.11", {"start": v(176.4, 86) * mm, "mid": v(177.1, 86.3) * mm, "end": v(177.4, 87) * mm});
            skArc(sketch, "E7.18.1.12", {"start": v(157.4, 87) * mm, "mid": v(157.7, 86.3) * mm, "end": v(158.4, 86) * mm});
            skArc(sketch, "E7.18.1.13", {"start": v(158.4, 110) * mm, "mid": v(157.7, 109.7) * mm, "end": v(157.4, 109) * mm});
            skLineSegment(sketch, "E7.18.2.0", {"start": v(177.4, 73) * mm, "end": v(157.4, 73) * mm, "construction": true});
            skPoint(sketch, "E7.18.2.1", {"position": v(157.4, 85) * mm});
            skLineSegment(sketch, "E7.18.2.2", {"start": v(157.4, 84) * mm, "end": v(157.4, 62) * mm});
            skPoint(sketch, "E7.18.2.3", {"position": v(177.4, 85) * mm});
            skLineSegment(sketch, "E7.18.2.4", {"start": v(158.4, 61) * mm, "end": v(176.4, 61) * mm});
            skPoint(sketch, "E7.18.2.5", {"position": v(157.4, 61) * mm});
            skPoint(sketch, "E7.18.2.6", {"position": v(177.4, 61) * mm});
            skCircle(sketch, "E7.18.2.7", {"center": v(167.4, 73) * mm, "radius": 6.5 * mm});
            skLineSegment(sketch, "E7.18.2.8", {"start": v(158.4, 85) * mm, "end": v(176.4, 85) * mm});
            skLineSegment(sketch, "E7.18.2.9", {"start": v(177.4, 84) * mm, "end": v(177.4, 62) * mm});
            skArc(sketch, "E7.18.2.10", {"start": v(177.4, 84) * mm, "mid": v(177.1, 84.7) * mm, "end": v(176.4, 85) * mm});
            skArc(sketch, "E7.18.2.11", {"start": v(176.4, 61) * mm, "mid": v(177.1, 61.3) * mm, "end": v(177.4, 62) * mm});
            skArc(sketch, "E7.18.2.12", {"start": v(157.4, 62) * mm, "mid": v(157.7, 61.3) * mm, "end": v(158.4, 61) * mm});
            skArc(sketch, "E7.18.2.13", {"start": v(158.4, 85) * mm, "mid": v(157.7, 84.7) * mm, "end": v(157.4, 84) * mm});
            skLineSegment(sketch, "E7.19.0.0", {"start": v(199.2, 123) * mm, "end": v(179.2, 123) * mm, "construction": true});
            skPoint(sketch, "E7.19.0.1", {"position": v(179.2, 135) * mm});
            skLineSegment(sketch, "E7.19.0.2", {"start": v(179.2, 134) * mm, "end": v(179.2, 112) * mm});
            skPoint(sketch, "E7.19.0.3", {"position": v(199.2, 135) * mm});
            skLineSegment(sketch, "E7.19.0.4", {"start": v(180.2, 111) * mm, "end": v(198.2, 111) * mm});
            skPoint(sketch, "E7.19.0.5", {"position": v(179.2, 111) * mm});
            skPoint(sketch, "E7.19.0.6", {"position": v(199.2, 111) * mm});
            skCircle(sketch, "E7.19.0.7", {"center": v(189.2, 123) * mm, "radius": 6.5 * mm});
            skLineSegment(sketch, "E7.19.0.8", {"start": v(180.2, 135) * mm, "end": v(198.2, 135) * mm});
            skLineSegment(sketch, "E7.19.0.9", {"start": v(199.2, 134) * mm, "end": v(199.2, 112) * mm});
            skArc(sketch, "E7.19.0.10", {"start": v(199.2, 134) * mm, "mid": v(198.9, 134.7) * mm, "end": v(198.2, 135) * mm});
            skArc(sketch, "E7.19.0.11", {"start": v(198.2, 111) * mm, "mid": v(198.9, 111.3) * mm, "end": v(199.2, 112) * mm});
            skArc(sketch, "E7.19.0.12", {"start": v(179.2, 112) * mm, "mid": v(179.5, 111.3) * mm, "end": v(180.2, 111) * mm});
            skArc(sketch, "E7.19.0.13", {"start": v(180.2, 135) * mm, "mid": v(179.5, 134.7) * mm, "end": v(179.2, 134) * mm});
            skLineSegment(sketch, "E7.19.1.0", {"start": v(199.2, 98) * mm, "end": v(179.2, 98) * mm, "construction": true});
            skPoint(sketch, "E7.19.1.1", {"position": v(179.2, 110) * mm});
            skLineSegment(sketch, "E7.19.1.2", {"start": v(179.2, 109) * mm, "end": v(179.2, 87) * mm});
            skPoint(sketch, "E7.19.1.3", {"position": v(199.2, 110) * mm});
            skLineSegment(sketch, "E7.19.1.4", {"start": v(180.2, 86) * mm, "end": v(198.2, 86) * mm});
            skPoint(sketch, "E7.19.1.5", {"position": v(179.2, 86) * mm});
            skPoint(sketch, "E7.19.1.6", {"position": v(199.2, 86) * mm});
            skCircle(sketch, "E7.19.1.7", {"center": v(189.2, 98) * mm, "radius": 6.5 * mm});
            skLineSegment(sketch, "E7.19.1.8", {"start": v(180.2, 110) * mm, "end": v(198.2, 110) * mm});
            skLineSegment(sketch, "E7.19.1.9", {"start": v(199.2, 109) * mm, "end": v(199.2, 87) * mm});
            skArc(sketch, "E7.19.1.10", {"start": v(199.2, 109) * mm, "mid": v(198.9, 109.7) * mm, "end": v(198.2, 110) * mm});
            skArc(sketch, "E7.19.1.11", {"start": v(198.2, 86) * mm, "mid": v(198.9, 86.3) * mm, "end": v(199.2, 87) * mm});
            skArc(sketch, "E7.19.1.12", {"start": v(179.2, 87) * mm, "mid": v(179.5, 86.3) * mm, "end": v(180.2, 86) * mm});
            skArc(sketch, "E7.19.1.13", {"start": v(180.2, 110) * mm, "mid": v(179.5, 109.7) * mm, "end": v(179.2, 109) * mm});
            skLineSegment(sketch, "E7.19.2.0", {"start": v(199.2, 73) * mm, "end": v(179.2, 73) * mm, "construction": true});
            skPoint(sketch, "E7.19.2.1", {"position": v(179.2, 85) * mm});
            skLineSegment(sketch, "E7.19.2.2", {"start": v(179.2, 84) * mm, "end": v(179.2, 62) * mm});
            skPoint(sketch, "E7.19.2.3", {"position": v(199.2, 85) * mm});
            skLineSegment(sketch, "E7.19.2.4", {"start": v(180.2, 61) * mm, "end": v(198.2, 61) * mm});
            skPoint(sketch, "E7.19.2.5", {"position": v(179.2, 61) * mm});
            skPoint(sketch, "E7.19.2.6", {"position": v(199.2, 61) * mm});
            skCircle(sketch, "E7.19.2.7", {"center": v(189.2, 73) * mm, "radius": 6.5 * mm});
            skLineSegment(sketch, "E7.19.2.8", {"start": v(180.2, 85) * mm, "end": v(198.2, 85) * mm});
            skLineSegment(sketch, "E7.19.2.9", {"start": v(199.2, 84) * mm, "end": v(199.2, 62) * mm});
            skArc(sketch, "E7.19.2.10", {"start": v(199.2, 84) * mm, "mid": v(198.9, 84.7) * mm, "end": v(198.2, 85) * mm});
            skArc(sketch, "E7.19.2.11", {"start": v(198.2, 61) * mm, "mid": v(198.9, 61.3) * mm, "end": v(199.2, 62) * mm});
            skArc(sketch, "E7.19.2.12", {"start": v(179.2, 62) * mm, "mid": v(179.5, 61.3) * mm, "end": v(180.2, 61) * mm});
            skArc(sketch, "E7.19.2.13", {"start": v(180.2, 85) * mm, "mid": v(179.5, 84.7) * mm, "end": v(179.2, 84) * mm});
            skLineSegment(sketch, "E7.direction1", {"start": v(-235, 111) * mm, "end": v(-213.2, 111) * mm, "construction": true});
            skLineSegment(sketch, "E7.direction2", {"start": v(-235, 111) * mm, "end": v(-235, 86) * mm, "construction": true});
            skSolve(sketch);
        }
        {
            var Q0;
            Q0 = qSketchRegion(id + "F0", true);
            extrude(context, id + "F1", {"entities" : qUnion([Q0]), "depth" : 1.45 * mm, "offsetDistance" : 25 * mm});
        }
    });
